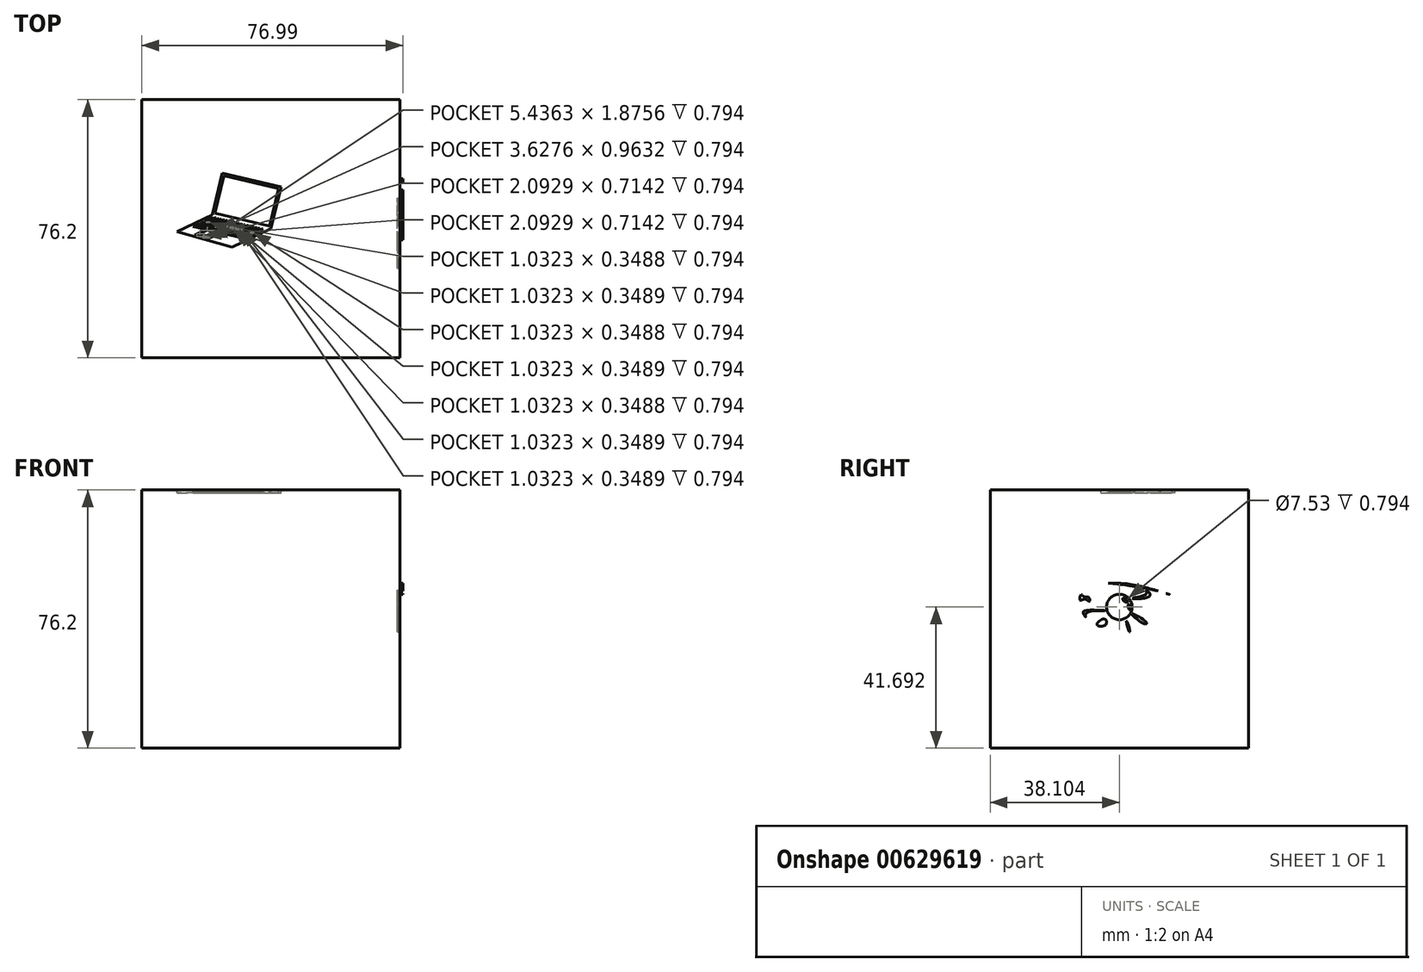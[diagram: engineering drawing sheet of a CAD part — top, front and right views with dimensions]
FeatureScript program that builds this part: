
annotation { "Feature Type Name" : "Feature", "Feature Type Description" : "" }
export const myFeature = defineFeature(function(context is Context, id is Id, definition is map)
    precondition{}
    {
        {
            var Q0;
            Q0=qCreatedBy(makeId("Top.planeOp"),FACE);
            var sketch = newSketch(context, id + "F0", { "sketchPlane" : qUnion([Q0])});
            skLineSegment(sketch, "E0", {"start": v(-11.48, -5.43) * mm, "end": v(0, 0) * mm});
            skLineSegment(sketch, "E1", {"start": v(0, 0) * mm, "end": v(2.93, 12.36) * mm});
            skLineSegment(sketch, "E2", {"start": v(2.93, 12.36) * mm, "end": v(-14.38, 16.45) * mm});
            skLineSegment(sketch, "E3", {"start": v(-14.38, 16.45) * mm, "end": v(-17.3, 4.1) * mm});
            skLineSegment(sketch, "E4", {"start": v(-17.3, 4.1) * mm, "end": v(0, 0) * mm});
            skLineSegment(sketch, "E5", {"start": v(-17.3, 4.1) * mm, "end": v(-27.71, -0.83) * mm});
            skLineSegment(sketch, "E6", {"start": v(-27.71, -0.83) * mm, "end": v(-11.48, -5.43) * mm});
            skLineSegment(sketch, "E7.0", {"start": v(-17.23, 3.43) * mm, "end": v(-16.37, 3.22) * mm});
            skLineSegment(sketch, "E7.1", {"start": v(-17.67, 3.22) * mm, "end": v(-18.38, 2.88) * mm});
            skLineSegment(sketch, "E7.2", {"start": v(-21.88, -1.83) * mm, "end": v(-20.42, -2.24) * mm});
            skLineSegment(sketch, "E7.3", {"start": v(-7.68, -2.93) * mm, "end": v(-6.94, -2.58) * mm});
            skLineSegment(sketch, "E8", {"start": v(-17.67, 3.22) * mm, "end": v(-17.08, 3.08) * mm});
            skLineSegment(sketch, "E9", {"start": v(-17.08, 3.08) * mm, "end": v(-16.64, 3.29) * mm});
            skPoint(sketch, "E10", {"position": v(-17.67, 3.22) * mm});
            skPoint(sketch, "E11", {"position": v(-17.23, 3.43) * mm});
            skPoint(sketch, "E12", {"position": v(-17.08, 3.08) * mm});
            skPoint(sketch, "E13", {"position": v(-16.64, 3.29) * mm});
            skPoint(sketch, "E14.1.0.0", {"position": v(-16.37, 3.22) * mm});
            skLineSegment(sketch, "E14.1.0.1", {"start": v(-16.8, 3.01) * mm, "end": v(-16.22, 2.87) * mm});
            skLineSegment(sketch, "E14.1.0.2", {"start": v(-16.22, 2.87) * mm, "end": v(-15.78, 3.08) * mm});
            skPoint(sketch, "E14.1.0.3", {"position": v(-16.22, 2.87) * mm});
            skPoint(sketch, "E14.1.0.4", {"position": v(-15.78, 3.08) * mm});
            skPoint(sketch, "E14.1.0.5", {"position": v(-16.8, 3.01) * mm});
            skPoint(sketch, "E14.2.0.0", {"position": v(-15.5, 3.02) * mm});
            skLineSegment(sketch, "E14.2.0.1", {"start": v(-15.94, 2.8) * mm, "end": v(-15.35, 2.67) * mm});
            skLineSegment(sketch, "E14.2.0.2", {"start": v(-15.35, 2.67) * mm, "end": v(-14.91, 2.88) * mm});
            skPoint(sketch, "E14.2.0.3", {"position": v(-15.35, 2.67) * mm});
            skPoint(sketch, "E14.2.0.4", {"position": v(-14.91, 2.88) * mm});
            skPoint(sketch, "E14.2.0.5", {"position": v(-15.94, 2.8) * mm});
            skPoint(sketch, "E14.3.0.0", {"position": v(-14.64, 2.81) * mm});
            skLineSegment(sketch, "E14.3.0.1", {"start": v(-15.08, 2.6) * mm, "end": v(-14.49, 2.46) * mm});
            skLineSegment(sketch, "E14.3.0.2", {"start": v(-14.49, 2.46) * mm, "end": v(-14.05, 2.67) * mm});
            skPoint(sketch, "E14.3.0.3", {"position": v(-14.49, 2.46) * mm});
            skPoint(sketch, "E14.3.0.4", {"position": v(-14.05, 2.67) * mm});
            skPoint(sketch, "E14.3.0.5", {"position": v(-15.08, 2.6) * mm});
            skPoint(sketch, "E14.4.0.0", {"position": v(-13.77, 2.6) * mm});
            skLineSegment(sketch, "E14.4.0.1", {"start": v(-14.21, 2.4) * mm, "end": v(-13.62, 2.26) * mm});
            skLineSegment(sketch, "E14.4.0.2", {"start": v(-13.62, 2.26) * mm, "end": v(-13.18, 2.47) * mm});
            skPoint(sketch, "E14.4.0.3", {"position": v(-13.62, 2.26) * mm});
            skPoint(sketch, "E14.4.0.4", {"position": v(-13.18, 2.47) * mm});
            skPoint(sketch, "E14.4.0.5", {"position": v(-14.21, 2.4) * mm});
            skPoint(sketch, "E14.5.0.0", {"position": v(-12.9, 2.4) * mm});
            skLineSegment(sketch, "E14.5.0.1", {"start": v(-13.35, 2.2) * mm, "end": v(-12.76, 2.05) * mm});
            skLineSegment(sketch, "E14.5.0.2", {"start": v(-12.76, 2.05) * mm, "end": v(-12.32, 2.26) * mm});
            skPoint(sketch, "E14.5.0.3", {"position": v(-12.76, 2.05) * mm});
            skPoint(sketch, "E14.5.0.4", {"position": v(-12.32, 2.26) * mm});
            skPoint(sketch, "E14.5.0.5", {"position": v(-13.35, 2.2) * mm});
            skPoint(sketch, "E14.6.0.0", {"position": v(-12.04, 2.2) * mm});
            skLineSegment(sketch, "E14.6.0.1", {"start": v(-12.48, 1.99) * mm, "end": v(-11.9, 1.85) * mm});
            skLineSegment(sketch, "E14.6.0.2", {"start": v(-11.9, 1.85) * mm, "end": v(-11.45, 2.06) * mm});
            skPoint(sketch, "E14.6.0.3", {"position": v(-11.9, 1.85) * mm});
            skPoint(sketch, "E14.6.0.4", {"position": v(-11.45, 2.06) * mm});
            skPoint(sketch, "E14.6.0.5", {"position": v(-12.48, 1.99) * mm});
            skPoint(sketch, "E14.7.0.0", {"position": v(-11.18, 2) * mm});
            skLineSegment(sketch, "E14.7.0.1", {"start": v(-11.62, 1.78) * mm, "end": v(-11.03, 1.64) * mm});
            skLineSegment(sketch, "E14.7.0.2", {"start": v(-11.03, 1.64) * mm, "end": v(-10.58, 1.85) * mm});
            skPoint(sketch, "E14.7.0.3", {"position": v(-11.03, 1.64) * mm});
            skPoint(sketch, "E14.7.0.4", {"position": v(-10.58, 1.85) * mm});
            skPoint(sketch, "E14.7.0.5", {"position": v(-11.62, 1.78) * mm});
            skPoint(sketch, "E14.8.0.0", {"position": v(-10.31, 1.79) * mm});
            skLineSegment(sketch, "E14.8.0.1", {"start": v(-10.75, 1.58) * mm, "end": v(-10.16, 1.44) * mm});
            skLineSegment(sketch, "E14.8.0.2", {"start": v(-10.16, 1.44) * mm, "end": v(-9.72, 1.65) * mm});
            skPoint(sketch, "E14.8.0.3", {"position": v(-10.16, 1.44) * mm});
            skPoint(sketch, "E14.8.0.4", {"position": v(-9.72, 1.65) * mm});
            skPoint(sketch, "E14.8.0.5", {"position": v(-10.75, 1.58) * mm});
            skPoint(sketch, "E14.9.0.0", {"position": v(-9.45, 1.58) * mm});
            skLineSegment(sketch, "E14.9.0.1", {"start": v(-9.89, 1.37) * mm, "end": v(-9.3, 1.23) * mm});
            skLineSegment(sketch, "E14.9.0.2", {"start": v(-9.3, 1.23) * mm, "end": v(-8.85, 1.44) * mm});
            skPoint(sketch, "E14.9.0.3", {"position": v(-9.3, 1.23) * mm});
            skPoint(sketch, "E14.9.0.4", {"position": v(-8.85, 1.44) * mm});
            skPoint(sketch, "E14.9.0.5", {"position": v(-9.89, 1.37) * mm});
            skPoint(sketch, "E14.10.0.0", {"position": v(-8.58, 1.38) * mm});
            skLineSegment(sketch, "E14.10.0.1", {"start": v(-9.02, 1.17) * mm, "end": v(-8.43, 1.03) * mm});
            skLineSegment(sketch, "E14.10.0.2", {"start": v(-8.43, 1.03) * mm, "end": v(-7.99, 1.24) * mm});
            skPoint(sketch, "E14.10.0.3", {"position": v(-8.43, 1.03) * mm});
            skPoint(sketch, "E14.10.0.4", {"position": v(-7.99, 1.24) * mm});
            skPoint(sketch, "E14.10.0.5", {"position": v(-9.02, 1.17) * mm});
            skPoint(sketch, "E14.11.0.0", {"position": v(-7.72, 1.17) * mm});
            skLineSegment(sketch, "E14.11.0.1", {"start": v(-8.16, 0.96) * mm, "end": v(-7.57, 0.83) * mm});
            skLineSegment(sketch, "E14.11.0.2", {"start": v(-7.57, 0.83) * mm, "end": v(-7.12, 1.03) * mm});
            skPoint(sketch, "E14.11.0.3", {"position": v(-7.57, 0.83) * mm});
            skPoint(sketch, "E14.11.0.4", {"position": v(-7.12, 1.03) * mm});
            skPoint(sketch, "E14.11.0.5", {"position": v(-8.16, 0.96) * mm});
            skPoint(sketch, "E14.12.0.0", {"position": v(-6.85, 0.97) * mm});
            skLineSegment(sketch, "E14.12.0.1", {"start": v(-7.3, 0.76) * mm, "end": v(-6.7, 0.62) * mm});
            skLineSegment(sketch, "E14.12.0.2", {"start": v(-6.7, 0.62) * mm, "end": v(-6.26, 0.83) * mm});
            skPoint(sketch, "E14.12.0.3", {"position": v(-6.7, 0.62) * mm});
            skPoint(sketch, "E14.12.0.4", {"position": v(-6.26, 0.83) * mm});
            skPoint(sketch, "E14.12.0.5", {"position": v(-7.3, 0.76) * mm});
            skPoint(sketch, "E14.13.0.0", {"position": v(-5.99, 0.76) * mm});
            skLineSegment(sketch, "E14.13.0.1", {"start": v(-6.43, 0.56) * mm, "end": v(-5.84, 0.42) * mm});
            skLineSegment(sketch, "E14.13.0.2", {"start": v(-5.84, 0.42) * mm, "end": v(-5.4, 0.62) * mm});
            skPoint(sketch, "E14.13.0.3", {"position": v(-5.84, 0.42) * mm});
            skPoint(sketch, "E14.13.0.4", {"position": v(-5.4, 0.62) * mm});
            skPoint(sketch, "E14.13.0.5", {"position": v(-6.43, 0.56) * mm});
            skPoint(sketch, "E14.14.0.0", {"position": v(-5.12, 0.56) * mm});
            skLineSegment(sketch, "E14.14.0.1", {"start": v(-5.56, 0.35) * mm, "end": v(-4.97, 0.21) * mm});
            skLineSegment(sketch, "E14.14.0.2", {"start": v(-4.97, 0.21) * mm, "end": v(-4.53, 0.42) * mm});
            skPoint(sketch, "E14.14.0.3", {"position": v(-4.97, 0.21) * mm});
            skPoint(sketch, "E14.14.0.4", {"position": v(-4.53, 0.42) * mm});
            skPoint(sketch, "E14.14.0.5", {"position": v(-5.56, 0.35) * mm});
            skPoint(sketch, "E14.15.0.0", {"position": v(-4.26, 0.35) * mm});
            skLineSegment(sketch, "E14.15.0.1", {"start": v(-4.7, 0.15) * mm, "end": v(-4.1, 0) * mm});
            skLineSegment(sketch, "E14.15.0.2", {"start": v(-4.1, 0) * mm, "end": v(-3.66, 0.21) * mm});
            skPoint(sketch, "E14.15.0.3", {"position": v(-4.1, 0) * mm});
            skPoint(sketch, "E14.15.0.4", {"position": v(-3.66, 0.21) * mm});
            skPoint(sketch, "E14.15.0.5", {"position": v(-4.7, 0.15) * mm});
            skPoint(sketch, "E14.16.0.0", {"position": v(-3.39, 0.15) * mm});
            skLineSegment(sketch, "E14.16.0.1", {"start": v(-3.83, -0.06) * mm, "end": v(-3.24, -0.2) * mm});
            skLineSegment(sketch, "E14.16.0.2", {"start": v(-3.24, -0.2) * mm, "end": v(-2.8, 0.01) * mm});
            skPoint(sketch, "E14.16.0.3", {"position": v(-3.24, -0.2) * mm});
            skPoint(sketch, "E14.16.0.4", {"position": v(-2.8, 0.01) * mm});
            skPoint(sketch, "E14.16.0.5", {"position": v(-3.83, -0.06) * mm});
            skPoint(sketch, "E14.17.0.0", {"position": v(-2.52, -0.05) * mm});
            skLineSegment(sketch, "E14.17.0.1", {"start": v(-2.97, -0.26) * mm, "end": v(-2.38, -0.4) * mm});
            skPoint(sketch, "E14.17.0.3", {"position": v(-2.38, -0.4) * mm});
            skPoint(sketch, "E14.17.0.4", {"position": v(-1.93, -0.2) * mm});
            skPoint(sketch, "E14.17.0.5", {"position": v(-2.97, -0.26) * mm});
            skLineSegment(sketch, "E14.direction1", {"start": v(-16.64, 3.29) * mm, "end": v(-16.37, 3.22) * mm, "construction": true});
            skLineSegment(sketch, "E15", {"start": v(-16.8, 3.01) * mm, "end": v(-16.37, 3.22) * mm});
            skLineSegment(sketch, "E16", {"start": v(-15.94, 2.8) * mm, "end": v(-15.5, 3.02) * mm});
            skLineSegment(sketch, "E17", {"start": v(-15.08, 2.6) * mm, "end": v(-14.64, 2.81) * mm});
            skLineSegment(sketch, "E18", {"start": v(-14.21, 2.4) * mm, "end": v(-13.77, 2.6) * mm});
            skLineSegment(sketch, "E19", {"start": v(-13.35, 2.2) * mm, "end": v(-12.9, 2.4) * mm});
            skLineSegment(sketch, "E20", {"start": v(-12.48, 1.99) * mm, "end": v(-12.04, 2.2) * mm});
            skLineSegment(sketch, "E21", {"start": v(-11.62, 1.78) * mm, "end": v(-11.18, 2) * mm});
            skLineSegment(sketch, "E22", {"start": v(-10.75, 1.58) * mm, "end": v(-10.31, 1.79) * mm});
            skLineSegment(sketch, "E23", {"start": v(-9.89, 1.37) * mm, "end": v(-9.45, 1.58) * mm});
            skLineSegment(sketch, "E24", {"start": v(-9.02, 1.17) * mm, "end": v(-8.58, 1.38) * mm});
            skLineSegment(sketch, "E25", {"start": v(-8.16, 0.96) * mm, "end": v(-7.72, 1.17) * mm});
            skLineSegment(sketch, "E26", {"start": v(-7.3, 0.76) * mm, "end": v(-6.85, 0.97) * mm});
            skLineSegment(sketch, "E27", {"start": v(-6.43, 0.56) * mm, "end": v(-5.99, 0.76) * mm});
            skLineSegment(sketch, "E28", {"start": v(-5.56, 0.35) * mm, "end": v(-5.12, 0.56) * mm});
            skLineSegment(sketch, "E29", {"start": v(-4.7, 0.15) * mm, "end": v(-4.26, 0.35) * mm});
            skLineSegment(sketch, "E30", {"start": v(-3.83, -0.06) * mm, "end": v(-3.39, 0.15) * mm});
            skLineSegment(sketch, "E31", {"start": v(-2.97, -0.26) * mm, "end": v(-2.52, -0.05) * mm});
            skLineSegment(sketch, "E32", {"start": v(-2.38, -0.4) * mm, "end": v(-2.35, -0.4) * mm});
            skPoint(sketch, "E33.1.0.0", {"position": v(-13.9, 1.51) * mm});
            skPoint(sketch, "E33.1.0.1", {"position": v(-14.33, 1.92) * mm});
            skLineSegment(sketch, "E33.1.0.2", {"start": v(-11.9, 1.04) * mm, "end": v(-11.3, 0.9) * mm});
            skPoint(sketch, "E33.1.0.3", {"position": v(-17.36, 2.33) * mm});
            skPoint(sketch, "E33.1.0.4", {"position": v(-10.44, 0.7) * mm});
            skPoint(sketch, "E33.1.0.5", {"position": v(-18.23, 2.53) * mm});
            skPoint(sketch, "E33.1.0.6", {"position": v(-9.3, 0.42) * mm});
            skPoint(sketch, "E33.1.0.7", {"position": v(-16.23, 2.06) * mm});
            skPoint(sketch, "E33.1.0.8", {"position": v(-12.77, 1.24) * mm});
            skPoint(sketch, "E33.1.0.9", {"position": v(-14.5, 1.65) * mm});
            skPoint(sketch, "E33.1.0.10", {"position": v(-17.96, 2.47) * mm});
            skLineSegment(sketch, "E33.1.0.11", {"start": v(-15.36, 1.86) * mm, "end": v(-14.77, 1.72) * mm});
            skLineSegment(sketch, "E33.1.0.12", {"start": v(-12.77, 1.24) * mm, "end": v(-12.17, 1.1) * mm});
            skPoint(sketch, "E33.1.0.13", {"position": v(-14.92, 2.06) * mm});
            skPoint(sketch, "E33.1.0.14", {"position": v(-11.46, 1.24) * mm});
            skPoint(sketch, "E33.1.0.15", {"position": v(-11.3, 0.9) * mm});
            skPoint(sketch, "E33.1.0.16", {"position": v(-18.82, 2.67) * mm});
            skLineSegment(sketch, "E33.1.0.17", {"start": v(-11.03, 0.83) * mm, "end": v(-10.6, 1.04) * mm});
            skLineSegment(sketch, "E33.1.0.18", {"start": v(-13.63, 1.45) * mm, "end": v(-13.04, 1.3) * mm});
            skPoint(sketch, "E33.1.0.19", {"position": v(-16.92, 2.54) * mm});
            skPoint(sketch, "E33.1.0.20", {"position": v(-13.46, 1.72) * mm});
            skPoint(sketch, "E33.1.0.21", {"position": v(-11.03, 0.83) * mm});
            skPoint(sketch, "E33.1.0.22", {"position": v(-15.2, 2.13) * mm});
            skPoint(sketch, "E33.1.0.23", {"position": v(-16.06, 2.33) * mm});
            skPoint(sketch, "E33.1.0.24", {"position": v(-11.73, 1.3) * mm});
            skLineSegment(sketch, "E33.1.0.25", {"start": v(-16.23, 2.06) * mm, "end": v(-15.63, 1.92) * mm});
            skPoint(sketch, "E33.1.0.26", {"position": v(-12.6, 1.51) * mm});
            skPoint(sketch, "E33.1.0.27", {"position": v(-16.65, 2.47) * mm});
            skPoint(sketch, "E33.1.0.28", {"position": v(-13.19, 1.65) * mm});
            skPoint(sketch, "E33.1.0.29", {"position": v(-16.5, 2.12) * mm});
            skPoint(sketch, "E33.1.0.30", {"position": v(-13.04, 1.3) * mm});
            skLineSegment(sketch, "E33.1.0.31", {"start": v(-11.3, 0.9) * mm, "end": v(-10.87, 1.1) * mm});
            skPoint(sketch, "E33.1.0.32", {"position": v(-9.58, 0.49) * mm});
            skLineSegment(sketch, "E33.1.0.33", {"start": v(-11.03, 0.83) * mm, "end": v(-10.44, 0.7) * mm});
            skPoint(sketch, "E33.1.0.34", {"position": v(-14.77, 1.72) * mm});
            skPoint(sketch, "E33.1.0.35", {"position": v(-17.1, 2.26) * mm});
            skPoint(sketch, "E33.1.0.36", {"position": v(-13.63, 1.45) * mm});
            skLineSegment(sketch, "E33.1.0.37", {"start": v(-17.1, 2.26) * mm, "end": v(-16.5, 2.12) * mm});
            skLineSegment(sketch, "E33.1.0.38", {"start": v(-14.5, 1.65) * mm, "end": v(-13.9, 1.51) * mm});
            skPoint(sketch, "E33.1.0.39", {"position": v(-10.17, 0.63) * mm});
            skLineSegment(sketch, "E33.1.0.40", {"start": v(-17.96, 2.47) * mm, "end": v(-17.36, 2.33) * mm});
            skLineSegment(sketch, "E33.1.0.41", {"start": v(-10.17, 0.63) * mm, "end": v(-9.58, 0.49) * mm});
            skPoint(sketch, "E33.1.0.42", {"position": v(-14.05, 1.86) * mm});
            skPoint(sketch, "E33.1.0.43", {"position": v(-15.63, 1.92) * mm});
            skPoint(sketch, "E33.1.0.44", {"position": v(-15.78, 2.27) * mm});
            skPoint(sketch, "E33.1.0.45", {"position": v(-12.32, 1.45) * mm});
            skPoint(sketch, "E33.1.0.46", {"position": v(-15.36, 1.86) * mm});
            skPoint(sketch, "E33.1.0.47", {"position": v(-12.17, 1.1) * mm});
            skPoint(sketch, "E33.1.0.48", {"position": v(-11.9, 1.04) * mm});
            skPoint(sketch, "E33.1.0.49", {"position": v(-17.51, 2.68) * mm});
            skPoint(sketch, "E33.1.0.50", {"position": v(-18.38, 2.88) * mm});
            skPoint(sketch, "E33.1.0.51", {"position": v(-17.79, 2.74) * mm});
            skLineSegment(sketch, "E33.1.0.52", {"start": v(-13.04, 1.3) * mm, "end": v(-12.6, 1.51) * mm});
            skPoint(sketch, "E33.1.0.53", {"position": v(-9.14, 0.7) * mm});
            skLineSegment(sketch, "E33.1.0.54", {"start": v(-17.1, 2.26) * mm, "end": v(-16.65, 2.47) * mm});
            skLineSegment(sketch, "E33.1.0.55", {"start": v(-16.5, 2.12) * mm, "end": v(-16.06, 2.33) * mm});
            skLineSegment(sketch, "E33.1.0.56", {"start": v(-17.96, 2.47) * mm, "end": v(-17.51, 2.68) * mm});
            skLineSegment(sketch, "E33.1.0.57", {"start": v(-12.77, 1.24) * mm, "end": v(-12.32, 1.45) * mm});
            skLineSegment(sketch, "E33.1.0.58", {"start": v(-14.77, 1.72) * mm, "end": v(-14.33, 1.92) * mm});
            skLineSegment(sketch, "E33.1.0.59", {"start": v(-18.23, 2.53) * mm, "end": v(-17.79, 2.74) * mm});
            skLineSegment(sketch, "E33.1.0.60", {"start": v(-15.63, 1.92) * mm, "end": v(-15.2, 2.13) * mm});
            skLineSegment(sketch, "E33.1.0.61", {"start": v(-14.5, 1.65) * mm, "end": v(-14.05, 1.86) * mm});
            skLineSegment(sketch, "E33.1.0.62", {"start": v(-12.17, 1.1) * mm, "end": v(-11.73, 1.3) * mm});
            skLineSegment(sketch, "E33.1.0.63", {"start": v(-15.36, 1.86) * mm, "end": v(-14.92, 2.06) * mm});
            skLineSegment(sketch, "E33.1.0.64", {"start": v(-16.23, 2.06) * mm, "end": v(-15.78, 2.27) * mm});
            skLineSegment(sketch, "E33.1.0.65", {"start": v(-13.63, 1.45) * mm, "end": v(-13.19, 1.65) * mm});
            skLineSegment(sketch, "E33.1.0.66", {"start": v(-17.36, 2.33) * mm, "end": v(-16.92, 2.54) * mm});
            skLineSegment(sketch, "E33.1.0.67", {"start": v(-11.9, 1.04) * mm, "end": v(-11.46, 1.24) * mm});
            skLineSegment(sketch, "E33.1.0.68", {"start": v(-13.9, 1.51) * mm, "end": v(-13.46, 1.72) * mm});
            skPoint(sketch, "E33.1.0.69", {"position": v(-8.86, 0.63) * mm});
            skLineSegment(sketch, "E33.1.0.70", {"start": v(-18.82, 2.67) * mm, "end": v(-18.23, 2.53) * mm});
            skPoint(sketch, "E33.1.0.71", {"position": v(-10.87, 1.1) * mm});
            skPoint(sketch, "E33.1.0.72", {"position": v(-10.6, 1.04) * mm});
            skLineSegment(sketch, "E33.1.0.73", {"start": v(-10.44, 0.7) * mm, "end": v(-10, 0.9) * mm});
            skPoint(sketch, "E33.1.0.74", {"position": v(-10, 0.9) * mm});
            skPoint(sketch, "E33.1.0.75", {"position": v(-9.73, 0.84) * mm});
            skLineSegment(sketch, "E33.1.0.76", {"start": v(-10.17, 0.63) * mm, "end": v(-9.73, 0.84) * mm});
            skLineSegment(sketch, "E33.1.0.77", {"start": v(-9.58, 0.49) * mm, "end": v(-9.14, 0.7) * mm});
            skLineSegment(sketch, "E33.1.0.78", {"start": v(-9.3, 0.42) * mm, "end": v(-8.86, 0.63) * mm});
            skLineSegment(sketch, "E33.1.0.79", {"start": v(-9.3, 0.42) * mm, "end": v(-8.71, 0.28) * mm});
            skLineSegment(sketch, "E33.1.0.80", {"start": v(-8.71, 0.28) * mm, "end": v(-8.27, 0.5) * mm});
            skLineSegment(sketch, "E33.1.0.81", {"start": v(-8.44, 0.22) * mm, "end": v(-8, 0.43) * mm});
            skLineSegment(sketch, "E33.1.0.82", {"start": v(-8.44, 0.22) * mm, "end": v(-7.85, 0.08) * mm});
            skLineSegment(sketch, "E33.1.0.83", {"start": v(-7.85, 0.08) * mm, "end": v(-7.4, 0.29) * mm});
            skPoint(sketch, "E33.1.0.84", {"position": v(-7.85, 0.08) * mm});
            skPoint(sketch, "E33.1.0.85", {"position": v(-8.44, 0.22) * mm});
            skPoint(sketch, "E33.1.0.86", {"position": v(-8.71, 0.28) * mm});
            skPoint(sketch, "E33.1.0.87", {"position": v(-8.27, 0.5) * mm});
            skPoint(sketch, "E33.1.0.88", {"position": v(-8, 0.43) * mm});
            skPoint(sketch, "E33.1.0.89", {"position": v(-7.4, 0.29) * mm});
            skPoint(sketch, "E33.1.0.90", {"position": v(-6.54, 0.08) * mm});
            skPoint(sketch, "E33.1.0.91", {"position": v(-5.84, -0.4) * mm});
            skLineSegment(sketch, "E33.1.0.92", {"start": v(-7.57, 0.01) * mm, "end": v(-7.13, 0.22) * mm});
            skLineSegment(sketch, "E33.1.0.93", {"start": v(-4.98, -0.6) * mm, "end": v(-4.39, -0.74) * mm});
            skLineSegment(sketch, "E33.1.0.94", {"start": v(-6.12, -0.33) * mm, "end": v(-5.68, -0.12) * mm});
            skLineSegment(sketch, "E33.1.0.95", {"start": v(-5.84, -0.4) * mm, "end": v(-5.25, -0.54) * mm});
            skPoint(sketch, "E33.1.0.96", {"position": v(-4.11, -0.8) * mm});
            skLineSegment(sketch, "E33.1.0.97", {"start": v(-5.25, -0.54) * mm, "end": v(-4.81, -0.33) * mm});
            skPoint(sketch, "E33.1.0.98", {"position": v(-6.27, 0.02) * mm});
            skPoint(sketch, "E33.1.0.99", {"position": v(-5.68, -0.12) * mm});
            skPoint(sketch, "E33.1.0.100", {"position": v(-6.12, -0.33) * mm});
            skPoint(sketch, "E33.1.0.101", {"position": v(-4.39, -0.74) * mm});
            skLineSegment(sketch, "E33.1.0.102", {"start": v(-4.98, -0.6) * mm, "end": v(-4.54, -0.4) * mm});
            skLineSegment(sketch, "E33.1.0.103", {"start": v(-4.11, -0.8) * mm, "end": v(-3.52, -0.95) * mm});
            skLineSegment(sketch, "E33.1.0.104", {"start": v(-6.98, -0.13) * mm, "end": v(-6.54, 0.08) * mm});
            skLineSegment(sketch, "E33.1.0.105", {"start": v(-4.11, -0.8) * mm, "end": v(-3.67, -0.6) * mm});
            skLineSegment(sketch, "E33.1.0.106", {"start": v(-4.39, -0.74) * mm, "end": v(-3.95, -0.53) * mm});
            skLineSegment(sketch, "E33.1.0.107", {"start": v(-6.7, -0.2) * mm, "end": v(-6.27, 0.02) * mm});
            skLineSegment(sketch, "E33.1.0.108", {"start": v(-5.84, -0.4) * mm, "end": v(-5.4, -0.19) * mm});
            skPoint(sketch, "E33.1.0.109", {"position": v(-7.13, 0.22) * mm});
            skPoint(sketch, "E33.1.0.110", {"position": v(-5.4, -0.19) * mm});
            skPoint(sketch, "E33.1.0.111", {"position": v(-5.25, -0.54) * mm});
            skPoint(sketch, "E33.1.0.112", {"position": v(-4.98, -0.6) * mm});
            skLineSegment(sketch, "E33.1.0.113", {"start": v(-6.7, -0.2) * mm, "end": v(-6.12, -0.33) * mm});
            skPoint(sketch, "E33.1.0.114", {"position": v(-6.7, -0.2) * mm});
            skPoint(sketch, "E33.1.0.115", {"position": v(-6.98, -0.13) * mm});
            skLineSegment(sketch, "E33.1.0.116", {"start": v(-7.57, 0.01) * mm, "end": v(-6.98, -0.13) * mm});
            skPoint(sketch, "E33.1.0.117", {"position": v(-7.57, 0.01) * mm});
            skPoint(sketch, "E33.1.0.118", {"position": v(-4.81, -0.33) * mm});
            skPoint(sketch, "E33.1.0.119", {"position": v(-4.54, -0.4) * mm});
            skPoint(sketch, "E33.1.0.120", {"position": v(-3.95, -0.53) * mm});
            skPoint(sketch, "E33.1.0.121", {"position": v(-3.67, -0.6) * mm});
            skPoint(sketch, "E33.1.0.122", {"position": v(-3.52, -0.95) * mm});
            skPoint(sketch, "E33.1.0.123", {"position": v(-3.08, -0.74) * mm});
            skPoint(sketch, "E33.2.0.0", {"position": v(-15.05, 0.97) * mm});
            skPoint(sketch, "E33.2.0.1", {"position": v(-15.48, 1.38) * mm});
            skLineSegment(sketch, "E33.2.0.2", {"start": v(-13.05, 0.5) * mm, "end": v(-12.46, 0.35) * mm});
            skPoint(sketch, "E33.2.0.3", {"position": v(-18.51, 1.79) * mm});
            skPoint(sketch, "E33.2.0.4", {"position": v(-11.6, 0.15) * mm});
            skPoint(sketch, "E33.2.0.5", {"position": v(-19.38, 2) * mm});
            skPoint(sketch, "E33.2.0.6", {"position": v(-10.45, -0.12) * mm});
            skPoint(sketch, "E33.2.0.7", {"position": v(-17.37, 1.52) * mm});
            skPoint(sketch, "E33.2.0.8", {"position": v(-13.91, 0.7) * mm});
            skPoint(sketch, "E33.2.0.9", {"position": v(-15.64, 1.1) * mm});
            skPoint(sketch, "E33.2.0.10", {"position": v(-19.1, 1.93) * mm});
            skLineSegment(sketch, "E33.2.0.11", {"start": v(-16.5, 1.31) * mm, "end": v(-15.92, 1.17) * mm});
            skLineSegment(sketch, "E33.2.0.12", {"start": v(-13.91, 0.7) * mm, "end": v(-13.32, 0.56) * mm});
            skPoint(sketch, "E33.2.0.13", {"position": v(-16.07, 1.52) * mm});
            skPoint(sketch, "E33.2.0.14", {"position": v(-12.6, 0.7) * mm});
            skPoint(sketch, "E33.2.0.15", {"position": v(-12.46, 0.35) * mm});
            skPoint(sketch, "E33.2.0.16", {"position": v(-19.97, 2.13) * mm});
            skLineSegment(sketch, "E33.2.0.17", {"start": v(-12.18, 0.29) * mm, "end": v(-11.74, 0.5) * mm});
            skLineSegment(sketch, "E33.2.0.18", {"start": v(-14.78, 0.9) * mm, "end": v(-14.19, 0.76) * mm});
            skPoint(sketch, "E33.2.0.19", {"position": v(-18.07, 2) * mm});
            skPoint(sketch, "E33.2.0.20", {"position": v(-14.61, 1.18) * mm});
            skPoint(sketch, "E33.2.0.21", {"position": v(-12.18, 0.29) * mm});
            skPoint(sketch, "E33.2.0.22", {"position": v(-16.34, 1.59) * mm});
            skPoint(sketch, "E33.2.0.23", {"position": v(-17.2, 1.8) * mm});
            skPoint(sketch, "E33.2.0.24", {"position": v(-12.88, 0.77) * mm});
            skLineSegment(sketch, "E33.2.0.25", {"start": v(-17.37, 1.52) * mm, "end": v(-16.78, 1.38) * mm});
            skPoint(sketch, "E33.2.0.26", {"position": v(-13.75, 0.97) * mm});
            skPoint(sketch, "E33.2.0.27", {"position": v(-17.8, 1.93) * mm});
            skPoint(sketch, "E33.2.0.28", {"position": v(-14.34, 1.11) * mm});
            skPoint(sketch, "E33.2.0.29", {"position": v(-17.65, 1.58) * mm});
            skPoint(sketch, "E33.2.0.30", {"position": v(-14.19, 0.76) * mm});
            skLineSegment(sketch, "E33.2.0.31", {"start": v(-12.46, 0.35) * mm, "end": v(-12.02, 0.56) * mm});
            skPoint(sketch, "E33.2.0.32", {"position": v(-10.73, -0.06) * mm});
            skLineSegment(sketch, "E33.2.0.33", {"start": v(-12.18, 0.29) * mm, "end": v(-11.6, 0.15) * mm});
            skPoint(sketch, "E33.2.0.34", {"position": v(-15.92, 1.17) * mm});
            skPoint(sketch, "E33.2.0.35", {"position": v(-18.24, 1.72) * mm});
            skPoint(sketch, "E33.2.0.36", {"position": v(-14.78, 0.9) * mm});
            skLineSegment(sketch, "E33.2.0.37", {"start": v(-18.24, 1.72) * mm, "end": v(-17.65, 1.58) * mm});
            skLineSegment(sketch, "E33.2.0.38", {"start": v(-15.64, 1.1) * mm, "end": v(-15.05, 0.97) * mm});
            skPoint(sketch, "E33.2.0.39", {"position": v(-11.32, 0.08) * mm});
            skLineSegment(sketch, "E33.2.0.40", {"start": v(-19.1, 1.93) * mm, "end": v(-18.51, 1.79) * mm});
            skLineSegment(sketch, "E33.2.0.41", {"start": v(-11.32, 0.08) * mm, "end": v(-10.73, -0.06) * mm});
            skPoint(sketch, "E33.2.0.42", {"position": v(-15.2, 1.32) * mm});
            skPoint(sketch, "E33.2.0.43", {"position": v(-16.78, 1.38) * mm});
            skPoint(sketch, "E33.2.0.44", {"position": v(-16.93, 1.73) * mm});
            skPoint(sketch, "E33.2.0.45", {"position": v(-13.47, 0.9) * mm});
            skPoint(sketch, "E33.2.0.46", {"position": v(-16.5, 1.31) * mm});
            skPoint(sketch, "E33.2.0.47", {"position": v(-13.32, 0.56) * mm});
            skPoint(sketch, "E33.2.0.48", {"position": v(-13.05, 0.5) * mm});
            skPoint(sketch, "E33.2.0.49", {"position": v(-18.66, 2.13) * mm});
            skPoint(sketch, "E33.2.0.50", {"position": v(-19.53, 2.34) * mm});
            skPoint(sketch, "E33.2.0.51", {"position": v(-18.94, 2.2) * mm});
            skLineSegment(sketch, "E33.2.0.52", {"start": v(-14.19, 0.76) * mm, "end": v(-13.75, 0.97) * mm});
            skPoint(sketch, "E33.2.0.53", {"position": v(-10.29, 0.15) * mm});
            skLineSegment(sketch, "E33.2.0.54", {"start": v(-18.24, 1.72) * mm, "end": v(-17.8, 1.93) * mm});
            skLineSegment(sketch, "E33.2.0.55", {"start": v(-17.65, 1.58) * mm, "end": v(-17.2, 1.8) * mm});
            skLineSegment(sketch, "E33.2.0.56", {"start": v(-19.1, 1.93) * mm, "end": v(-18.66, 2.13) * mm});
            skLineSegment(sketch, "E33.2.0.57", {"start": v(-13.91, 0.7) * mm, "end": v(-13.47, 0.9) * mm});
            skLineSegment(sketch, "E33.2.0.58", {"start": v(-15.92, 1.17) * mm, "end": v(-15.48, 1.38) * mm});
            skLineSegment(sketch, "E33.2.0.59", {"start": v(-19.38, 2) * mm, "end": v(-18.94, 2.2) * mm});
            skLineSegment(sketch, "E33.2.0.60", {"start": v(-16.78, 1.38) * mm, "end": v(-16.34, 1.59) * mm});
            skLineSegment(sketch, "E33.2.0.61", {"start": v(-15.64, 1.1) * mm, "end": v(-15.2, 1.32) * mm});
            skLineSegment(sketch, "E33.2.0.62", {"start": v(-13.32, 0.56) * mm, "end": v(-12.88, 0.77) * mm});
            skLineSegment(sketch, "E33.2.0.63", {"start": v(-16.5, 1.31) * mm, "end": v(-16.07, 1.52) * mm});
            skLineSegment(sketch, "E33.2.0.64", {"start": v(-17.37, 1.52) * mm, "end": v(-16.93, 1.73) * mm});
            skLineSegment(sketch, "E33.2.0.65", {"start": v(-14.78, 0.9) * mm, "end": v(-14.34, 1.11) * mm});
            skLineSegment(sketch, "E33.2.0.66", {"start": v(-18.51, 1.79) * mm, "end": v(-18.07, 2) * mm});
            skLineSegment(sketch, "E33.2.0.67", {"start": v(-13.05, 0.5) * mm, "end": v(-12.6, 0.7) * mm});
            skLineSegment(sketch, "E33.2.0.68", {"start": v(-15.05, 0.97) * mm, "end": v(-14.61, 1.18) * mm});
            skPoint(sketch, "E33.2.0.69", {"position": v(-10.01, 0.09) * mm});
            skLineSegment(sketch, "E33.2.0.70", {"start": v(-19.97, 2.13) * mm, "end": v(-19.38, 2) * mm});
            skPoint(sketch, "E33.2.0.71", {"position": v(-12.02, 0.56) * mm});
            skPoint(sketch, "E33.2.0.72", {"position": v(-11.74, 0.5) * mm});
            skLineSegment(sketch, "E33.2.0.73", {"start": v(-11.6, 0.15) * mm, "end": v(-11.15, 0.36) * mm});
            skPoint(sketch, "E33.2.0.74", {"position": v(-11.15, 0.36) * mm});
            skPoint(sketch, "E33.2.0.75", {"position": v(-10.88, 0.3) * mm});
            skLineSegment(sketch, "E33.2.0.76", {"start": v(-11.32, 0.08) * mm, "end": v(-10.88, 0.3) * mm});
            skLineSegment(sketch, "E33.2.0.77", {"start": v(-10.73, -0.06) * mm, "end": v(-10.29, 0.15) * mm});
            skLineSegment(sketch, "E33.2.0.78", {"start": v(-10.45, -0.12) * mm, "end": v(-10.01, 0.09) * mm});
            skLineSegment(sketch, "E33.2.0.79", {"start": v(-10.45, -0.12) * mm, "end": v(-9.86, -0.26) * mm});
            skLineSegment(sketch, "E33.2.0.80", {"start": v(-9.86, -0.26) * mm, "end": v(-9.42, -0.05) * mm});
            skLineSegment(sketch, "E33.2.0.81", {"start": v(-9.59, -0.33) * mm, "end": v(-9.15, -0.12) * mm});
            skLineSegment(sketch, "E33.2.0.82", {"start": v(-9.59, -0.33) * mm, "end": v(-9, -0.47) * mm});
            skLineSegment(sketch, "E33.2.0.83", {"start": v(-9, -0.47) * mm, "end": v(-8.56, -0.26) * mm});
            skPoint(sketch, "E33.2.0.84", {"position": v(-9, -0.47) * mm});
            skPoint(sketch, "E33.2.0.85", {"position": v(-9.59, -0.33) * mm});
            skPoint(sketch, "E33.2.0.86", {"position": v(-9.86, -0.26) * mm});
            skPoint(sketch, "E33.2.0.87", {"position": v(-9.42, -0.05) * mm});
            skPoint(sketch, "E33.2.0.88", {"position": v(-9.15, -0.12) * mm});
            skPoint(sketch, "E33.2.0.89", {"position": v(-8.56, -0.26) * mm});
            skPoint(sketch, "E33.2.0.90", {"position": v(-7.7, -0.46) * mm});
            skPoint(sketch, "E33.2.0.91", {"position": v(-7, -0.94) * mm});
            skLineSegment(sketch, "E33.2.0.92", {"start": v(-8.72, -0.53) * mm, "end": v(-8.28, -0.32) * mm});
            skLineSegment(sketch, "E33.2.0.93", {"start": v(-6.13, -1.15) * mm, "end": v(-5.54, -1.29) * mm});
            skLineSegment(sketch, "E33.2.0.94", {"start": v(-7.27, -0.88) * mm, "end": v(-6.83, -0.67) * mm});
            skLineSegment(sketch, "E33.2.0.95", {"start": v(-7, -0.94) * mm, "end": v(-6.4, -1.08) * mm});
            skPoint(sketch, "E33.2.0.96", {"position": v(-5.26, -1.35) * mm});
            skLineSegment(sketch, "E33.2.0.97", {"start": v(-6.4, -1.08) * mm, "end": v(-5.96, -0.87) * mm});
            skPoint(sketch, "E33.2.0.98", {"position": v(-7.42, -0.53) * mm});
            skPoint(sketch, "E33.2.0.99", {"position": v(-6.83, -0.67) * mm});
            skPoint(sketch, "E33.2.0.100", {"position": v(-7.27, -0.88) * mm});
            skPoint(sketch, "E33.2.0.101", {"position": v(-5.54, -1.29) * mm});
            skLineSegment(sketch, "E33.2.0.102", {"start": v(-6.13, -1.15) * mm, "end": v(-5.69, -0.94) * mm});
            skLineSegment(sketch, "E33.2.0.103", {"start": v(-5.26, -1.35) * mm, "end": v(-4.67, -1.5) * mm});
            skLineSegment(sketch, "E33.2.0.104", {"start": v(-8.13, -0.67) * mm, "end": v(-7.7, -0.46) * mm});
            skLineSegment(sketch, "E33.2.0.105", {"start": v(-5.26, -1.35) * mm, "end": v(-4.82, -1.14) * mm});
            skLineSegment(sketch, "E33.2.0.106", {"start": v(-5.54, -1.29) * mm, "end": v(-5.1, -1.08) * mm});
            skLineSegment(sketch, "E33.2.0.107", {"start": v(-7.86, -0.74) * mm, "end": v(-7.42, -0.53) * mm});
            skLineSegment(sketch, "E33.2.0.108", {"start": v(-7, -0.94) * mm, "end": v(-6.55, -0.73) * mm});
            skPoint(sketch, "E33.2.0.109", {"position": v(-8.28, -0.32) * mm});
            skPoint(sketch, "E33.2.0.110", {"position": v(-6.55, -0.73) * mm});
            skPoint(sketch, "E33.2.0.111", {"position": v(-6.4, -1.08) * mm});
            skPoint(sketch, "E33.2.0.112", {"position": v(-6.13, -1.15) * mm});
            skLineSegment(sketch, "E33.2.0.113", {"start": v(-7.86, -0.74) * mm, "end": v(-7.27, -0.88) * mm});
            skPoint(sketch, "E33.2.0.114", {"position": v(-7.86, -0.74) * mm});
            skPoint(sketch, "E33.2.0.115", {"position": v(-8.13, -0.67) * mm});
            skLineSegment(sketch, "E33.2.0.116", {"start": v(-8.72, -0.53) * mm, "end": v(-8.13, -0.67) * mm});
            skPoint(sketch, "E33.2.0.117", {"position": v(-8.72, -0.53) * mm});
            skPoint(sketch, "E33.2.0.118", {"position": v(-5.96, -0.87) * mm});
            skPoint(sketch, "E33.2.0.119", {"position": v(-5.69, -0.94) * mm});
            skPoint(sketch, "E33.2.0.120", {"position": v(-5.1, -1.08) * mm});
            skPoint(sketch, "E33.2.0.121", {"position": v(-4.82, -1.14) * mm});
            skPoint(sketch, "E33.2.0.122", {"position": v(-4.67, -1.5) * mm});
            skPoint(sketch, "E33.2.0.123", {"position": v(-4.23, -1.28) * mm});
            skPoint(sketch, "E33.3.0.0", {"position": v(-16.2, 0.42) * mm});
            skPoint(sketch, "E33.3.0.1", {"position": v(-16.62, 0.84) * mm});
            skLineSegment(sketch, "E33.3.0.2", {"start": v(-14.2, -0.05) * mm, "end": v(-13.6, -0.2) * mm});
            skPoint(sketch, "E33.3.0.3", {"position": v(-19.66, 1.24) * mm});
            skPoint(sketch, "E33.3.0.4", {"position": v(-12.74, -0.4) * mm});
            skPoint(sketch, "E33.3.0.5", {"position": v(-20.53, 1.45) * mm});
            skPoint(sketch, "E33.3.0.6", {"position": v(-11.6, -0.67) * mm});
            skPoint(sketch, "E33.3.0.7", {"position": v(-18.52, 0.97) * mm});
            skPoint(sketch, "E33.3.0.8", {"position": v(-15.06, 0.15) * mm});
            skPoint(sketch, "E33.3.0.9", {"position": v(-16.8, 0.56) * mm});
            skPoint(sketch, "E33.3.0.10", {"position": v(-20.25, 1.38) * mm});
            skLineSegment(sketch, "E33.3.0.11", {"start": v(-17.66, 0.77) * mm, "end": v(-17.07, 0.63) * mm});
            skLineSegment(sketch, "E33.3.0.12", {"start": v(-15.06, 0.15) * mm, "end": v(-14.47, 0.01) * mm});
            skPoint(sketch, "E33.3.0.13", {"position": v(-17.21, 0.98) * mm});
            skPoint(sketch, "E33.3.0.14", {"position": v(-13.75, 0.16) * mm});
            skPoint(sketch, "E33.3.0.15", {"position": v(-13.6, -0.2) * mm});
            skPoint(sketch, "E33.3.0.16", {"position": v(-21.12, 1.59) * mm});
            skLineSegment(sketch, "E33.3.0.17", {"start": v(-13.33, -0.26) * mm, "end": v(-12.89, -0.05) * mm});
            skLineSegment(sketch, "E33.3.0.18", {"start": v(-15.93, 0.36) * mm, "end": v(-15.34, 0.22) * mm});
            skPoint(sketch, "E33.3.0.19", {"position": v(-19.22, 1.45) * mm});
            skPoint(sketch, "E33.3.0.20", {"position": v(-15.76, 0.63) * mm});
            skPoint(sketch, "E33.3.0.21", {"position": v(-13.33, -0.26) * mm});
            skPoint(sketch, "E33.3.0.22", {"position": v(-17.49, 1.04) * mm});
            skPoint(sketch, "E33.3.0.23", {"position": v(-18.35, 1.25) * mm});
            skPoint(sketch, "E33.3.0.24", {"position": v(-14.03, 0.22) * mm});
            skLineSegment(sketch, "E33.3.0.25", {"start": v(-18.52, 0.97) * mm, "end": v(-17.93, 0.83) * mm});
            skPoint(sketch, "E33.3.0.26", {"position": v(-14.9, 0.43) * mm});
            skPoint(sketch, "E33.3.0.27", {"position": v(-18.94, 1.39) * mm});
            skPoint(sketch, "E33.3.0.28", {"position": v(-15.48, 0.57) * mm});
            skPoint(sketch, "E33.3.0.29", {"position": v(-18.8, 1.04) * mm});
            skPoint(sketch, "E33.3.0.30", {"position": v(-15.34, 0.22) * mm});
            skLineSegment(sketch, "E33.3.0.31", {"start": v(-13.6, -0.2) * mm, "end": v(-13.16, 0.02) * mm});
            skPoint(sketch, "E33.3.0.32", {"position": v(-11.87, -0.6) * mm});
            skLineSegment(sketch, "E33.3.0.33", {"start": v(-13.33, -0.26) * mm, "end": v(-12.74, -0.4) * mm});
            skPoint(sketch, "E33.3.0.34", {"position": v(-17.07, 0.63) * mm});
            skPoint(sketch, "E33.3.0.35", {"position": v(-19.39, 1.18) * mm});
            skPoint(sketch, "E33.3.0.36", {"position": v(-15.93, 0.36) * mm});
            skLineSegment(sketch, "E33.3.0.37", {"start": v(-19.39, 1.18) * mm, "end": v(-18.8, 1.04) * mm});
            skLineSegment(sketch, "E33.3.0.38", {"start": v(-16.8, 0.56) * mm, "end": v(-16.2, 0.42) * mm});
            skPoint(sketch, "E33.3.0.39", {"position": v(-12.47, -0.46) * mm});
            skLineSegment(sketch, "E33.3.0.40", {"start": v(-20.25, 1.38) * mm, "end": v(-19.66, 1.24) * mm});
            skLineSegment(sketch, "E33.3.0.41", {"start": v(-12.47, -0.46) * mm, "end": v(-11.87, -0.6) * mm});
            skPoint(sketch, "E33.3.0.42", {"position": v(-16.35, 0.77) * mm});
            skPoint(sketch, "E33.3.0.43", {"position": v(-17.93, 0.83) * mm});
            skPoint(sketch, "E33.3.0.44", {"position": v(-18.08, 1.18) * mm});
            skPoint(sketch, "E33.3.0.45", {"position": v(-14.62, 0.36) * mm});
            skPoint(sketch, "E33.3.0.46", {"position": v(-17.66, 0.77) * mm});
            skPoint(sketch, "E33.3.0.47", {"position": v(-14.47, 0.01) * mm});
            skPoint(sketch, "E33.3.0.48", {"position": v(-14.2, -0.05) * mm});
            skPoint(sketch, "E33.3.0.49", {"position": v(-19.8, 1.6) * mm});
            skPoint(sketch, "E33.3.0.50", {"position": v(-20.67, 1.8) * mm});
            skPoint(sketch, "E33.3.0.51", {"position": v(-20.08, 1.66) * mm});
            skLineSegment(sketch, "E33.3.0.52", {"start": v(-15.34, 0.22) * mm, "end": v(-14.9, 0.43) * mm});
            skPoint(sketch, "E33.3.0.53", {"position": v(-11.43, -0.4) * mm});
            skLineSegment(sketch, "E33.3.0.54", {"start": v(-19.39, 1.18) * mm, "end": v(-18.94, 1.39) * mm});
            skLineSegment(sketch, "E33.3.0.55", {"start": v(-18.8, 1.04) * mm, "end": v(-18.35, 1.25) * mm});
            skLineSegment(sketch, "E33.3.0.56", {"start": v(-20.25, 1.38) * mm, "end": v(-19.8, 1.6) * mm});
            skLineSegment(sketch, "E33.3.0.57", {"start": v(-15.06, 0.15) * mm, "end": v(-14.62, 0.36) * mm});
            skLineSegment(sketch, "E33.3.0.58", {"start": v(-17.07, 0.63) * mm, "end": v(-16.62, 0.84) * mm});
            skLineSegment(sketch, "E33.3.0.59", {"start": v(-20.53, 1.45) * mm, "end": v(-20.08, 1.66) * mm});
            skLineSegment(sketch, "E33.3.0.60", {"start": v(-17.93, 0.83) * mm, "end": v(-17.49, 1.04) * mm});
            skLineSegment(sketch, "E33.3.0.61", {"start": v(-16.8, 0.56) * mm, "end": v(-16.35, 0.77) * mm});
            skLineSegment(sketch, "E33.3.0.62", {"start": v(-14.47, 0.01) * mm, "end": v(-14.03, 0.22) * mm});
            skLineSegment(sketch, "E33.3.0.63", {"start": v(-17.66, 0.77) * mm, "end": v(-17.21, 0.98) * mm});
            skLineSegment(sketch, "E33.3.0.64", {"start": v(-18.52, 0.97) * mm, "end": v(-18.08, 1.18) * mm});
            skLineSegment(sketch, "E33.3.0.65", {"start": v(-15.93, 0.36) * mm, "end": v(-15.48, 0.57) * mm});
            skLineSegment(sketch, "E33.3.0.66", {"start": v(-19.66, 1.24) * mm, "end": v(-19.22, 1.45) * mm});
            skLineSegment(sketch, "E33.3.0.67", {"start": v(-14.2, -0.05) * mm, "end": v(-13.75, 0.16) * mm});
            skLineSegment(sketch, "E33.3.0.68", {"start": v(-16.2, 0.42) * mm, "end": v(-15.76, 0.63) * mm});
            skPoint(sketch, "E33.3.0.69", {"position": v(-11.16, -0.46) * mm});
            skLineSegment(sketch, "E33.3.0.70", {"start": v(-21.12, 1.59) * mm, "end": v(-20.53, 1.45) * mm});
            skPoint(sketch, "E33.3.0.71", {"position": v(-13.16, 0.02) * mm});
            skPoint(sketch, "E33.3.0.72", {"position": v(-12.89, -0.05) * mm});
            skLineSegment(sketch, "E33.3.0.73", {"start": v(-12.74, -0.4) * mm, "end": v(-12.3, -0.19) * mm});
            skPoint(sketch, "E33.3.0.74", {"position": v(-12.3, -0.19) * mm});
            skPoint(sketch, "E33.3.0.75", {"position": v(-12.02, -0.25) * mm});
            skLineSegment(sketch, "E33.3.0.76", {"start": v(-12.47, -0.46) * mm, "end": v(-12.02, -0.25) * mm});
            skLineSegment(sketch, "E33.3.0.77", {"start": v(-11.87, -0.6) * mm, "end": v(-11.43, -0.4) * mm});
            skLineSegment(sketch, "E33.3.0.78", {"start": v(-11.6, -0.67) * mm, "end": v(-11.16, -0.46) * mm});
            skLineSegment(sketch, "E33.3.0.79", {"start": v(-11.6, -0.67) * mm, "end": v(-11, -0.8) * mm});
            skLineSegment(sketch, "E33.3.0.80", {"start": v(-11, -0.8) * mm, "end": v(-10.57, -0.6) * mm});
            skLineSegment(sketch, "E33.3.0.81", {"start": v(-10.74, -0.87) * mm, "end": v(-10.3, -0.66) * mm});
            skLineSegment(sketch, "E33.3.0.82", {"start": v(-10.74, -0.87) * mm, "end": v(-10.14, -1) * mm});
            skLineSegment(sketch, "E33.3.0.83", {"start": v(-10.14, -1) * mm, "end": v(-9.7, -0.8) * mm});
            skPoint(sketch, "E33.3.0.84", {"position": v(-10.14, -1) * mm});
            skPoint(sketch, "E33.3.0.85", {"position": v(-10.74, -0.87) * mm});
            skPoint(sketch, "E33.3.0.86", {"position": v(-11, -0.8) * mm});
            skPoint(sketch, "E33.3.0.87", {"position": v(-10.57, -0.6) * mm});
            skPoint(sketch, "E33.3.0.88", {"position": v(-10.3, -0.66) * mm});
            skPoint(sketch, "E33.3.0.89", {"position": v(-9.7, -0.8) * mm});
            skPoint(sketch, "E33.3.0.90", {"position": v(-8.84, -1) * mm});
            skPoint(sketch, "E33.3.0.91", {"position": v(-8.14, -1.48) * mm});
            skLineSegment(sketch, "E33.3.0.92", {"start": v(-9.87, -1.07) * mm, "end": v(-9.43, -0.87) * mm});
            skLineSegment(sketch, "E33.3.0.93", {"start": v(-7.28, -1.69) * mm, "end": v(-6.68, -1.83) * mm});
            skLineSegment(sketch, "E33.3.0.94", {"start": v(-8.41, -1.42) * mm, "end": v(-7.97, -1.21) * mm});
            skLineSegment(sketch, "E33.3.0.95", {"start": v(-8.14, -1.48) * mm, "end": v(-7.55, -1.62) * mm});
            skPoint(sketch, "E33.3.0.96", {"position": v(-6.4, -1.9) * mm});
            skLineSegment(sketch, "E33.3.0.97", {"start": v(-7.55, -1.62) * mm, "end": v(-7.1, -1.42) * mm});
            skPoint(sketch, "E33.3.0.98", {"position": v(-8.56, -1.07) * mm});
            skPoint(sketch, "E33.3.0.99", {"position": v(-7.97, -1.21) * mm});
            skPoint(sketch, "E33.3.0.100", {"position": v(-8.41, -1.42) * mm});
            skPoint(sketch, "E33.3.0.101", {"position": v(-6.68, -1.83) * mm});
            skLineSegment(sketch, "E33.3.0.102", {"start": v(-7.28, -1.69) * mm, "end": v(-6.83, -1.48) * mm});
            skLineSegment(sketch, "E33.3.0.103", {"start": v(-6.4, -1.9) * mm, "end": v(-5.82, -2.03) * mm});
            skLineSegment(sketch, "E33.3.0.104", {"start": v(-9.28, -1.21) * mm, "end": v(-8.84, -1) * mm});
            skLineSegment(sketch, "E33.3.0.105", {"start": v(-6.4, -1.9) * mm, "end": v(-5.97, -1.69) * mm});
            skLineSegment(sketch, "E33.3.0.106", {"start": v(-6.68, -1.83) * mm, "end": v(-6.24, -1.62) * mm});
            skLineSegment(sketch, "E33.3.0.107", {"start": v(-9, -1.28) * mm, "end": v(-8.56, -1.07) * mm});
            skLineSegment(sketch, "E33.3.0.108", {"start": v(-8.14, -1.48) * mm, "end": v(-7.7, -1.28) * mm});
            skPoint(sketch, "E33.3.0.109", {"position": v(-9.43, -0.87) * mm});
            skPoint(sketch, "E33.3.0.110", {"position": v(-7.7, -1.28) * mm});
            skPoint(sketch, "E33.3.0.111", {"position": v(-7.55, -1.62) * mm});
            skPoint(sketch, "E33.3.0.112", {"position": v(-7.28, -1.69) * mm});
            skLineSegment(sketch, "E33.3.0.113", {"start": v(-9, -1.28) * mm, "end": v(-8.41, -1.42) * mm});
            skPoint(sketch, "E33.3.0.114", {"position": v(-9, -1.28) * mm});
            skPoint(sketch, "E33.3.0.115", {"position": v(-9.28, -1.21) * mm});
            skLineSegment(sketch, "E33.3.0.116", {"start": v(-9.87, -1.07) * mm, "end": v(-9.28, -1.21) * mm});
            skPoint(sketch, "E33.3.0.117", {"position": v(-9.87, -1.07) * mm});
            skPoint(sketch, "E33.3.0.118", {"position": v(-7.1, -1.42) * mm});
            skPoint(sketch, "E33.3.0.119", {"position": v(-6.83, -1.48) * mm});
            skPoint(sketch, "E33.3.0.120", {"position": v(-6.24, -1.62) * mm});
            skPoint(sketch, "E33.3.0.121", {"position": v(-5.97, -1.69) * mm});
            skPoint(sketch, "E33.3.0.122", {"position": v(-5.82, -2.03) * mm});
            skPoint(sketch, "E33.3.0.123", {"position": v(-5.38, -1.82) * mm});
            skPoint(sketch, "E33.4.0.0", {"position": v(-17.35, -0.12) * mm});
            skPoint(sketch, "E33.4.0.1", {"position": v(-17.77, 0.3) * mm});
            skLineSegment(sketch, "E33.4.0.2", {"start": v(-15.34, -0.6) * mm, "end": v(-14.75, -0.73) * mm});
            skPoint(sketch, "E33.4.0.3", {"position": v(-20.8, 0.7) * mm});
            skPoint(sketch, "E33.4.0.4", {"position": v(-13.89, -0.94) * mm});
            skPoint(sketch, "E33.4.0.5", {"position": v(-21.67, 0.9) * mm});
            skPoint(sketch, "E33.4.0.6", {"position": v(-12.75, -1.2) * mm});
            skPoint(sketch, "E33.4.0.7", {"position": v(-19.67, 0.43) * mm});
            skPoint(sketch, "E33.4.0.8", {"position": v(-16.2, -0.39) * mm});
            skPoint(sketch, "E33.4.0.9", {"position": v(-17.94, 0.02) * mm});
            skPoint(sketch, "E33.4.0.10", {"position": v(-21.4, 0.84) * mm});
            skLineSegment(sketch, "E33.4.0.11", {"start": v(-18.8, 0.22) * mm, "end": v(-18.21, 0.08) * mm});
            skLineSegment(sketch, "E33.4.0.12", {"start": v(-16.2, -0.39) * mm, "end": v(-15.62, -0.53) * mm});
            skPoint(sketch, "E33.4.0.13", {"position": v(-18.36, 0.43) * mm});
            skPoint(sketch, "E33.4.0.14", {"position": v(-14.9, -0.39) * mm});
            skPoint(sketch, "E33.4.0.15", {"position": v(-14.75, -0.73) * mm});
            skPoint(sketch, "E33.4.0.16", {"position": v(-22.26, 1.04) * mm});
            skLineSegment(sketch, "E33.4.0.17", {"start": v(-14.48, -0.8) * mm, "end": v(-14.04, -0.6) * mm});
            skLineSegment(sketch, "E33.4.0.18", {"start": v(-17.07, -0.18) * mm, "end": v(-16.48, -0.32) * mm});
            skPoint(sketch, "E33.4.0.19", {"position": v(-20.37, 0.9) * mm});
            skPoint(sketch, "E33.4.0.20", {"position": v(-16.9, 0.09) * mm});
            skPoint(sketch, "E33.4.0.21", {"position": v(-14.48, -0.8) * mm});
            skPoint(sketch, "E33.4.0.22", {"position": v(-18.64, 0.5) * mm});
            skPoint(sketch, "E33.4.0.23", {"position": v(-19.5, 0.7) * mm});
            skPoint(sketch, "E33.4.0.24", {"position": v(-15.18, -0.32) * mm});
            skLineSegment(sketch, "E33.4.0.25", {"start": v(-19.67, 0.43) * mm, "end": v(-19.08, 0.29) * mm});
            skPoint(sketch, "E33.4.0.26", {"position": v(-16.04, -0.12) * mm});
            skPoint(sketch, "E33.4.0.27", {"position": v(-20.1, 0.84) * mm});
            skPoint(sketch, "E33.4.0.28", {"position": v(-16.63, 0.02) * mm});
            skPoint(sketch, "E33.4.0.29", {"position": v(-19.94, 0.5) * mm});
            skPoint(sketch, "E33.4.0.30", {"position": v(-16.48, -0.32) * mm});
            skLineSegment(sketch, "E33.4.0.31", {"start": v(-14.75, -0.73) * mm, "end": v(-14.31, -0.53) * mm});
            skPoint(sketch, "E33.4.0.32", {"position": v(-13.02, -1.14) * mm});
            skLineSegment(sketch, "E33.4.0.33", {"start": v(-14.48, -0.8) * mm, "end": v(-13.89, -0.94) * mm});
            skPoint(sketch, "E33.4.0.34", {"position": v(-18.21, 0.08) * mm});
            skPoint(sketch, "E33.4.0.35", {"position": v(-20.53, 0.63) * mm});
            skPoint(sketch, "E33.4.0.36", {"position": v(-17.07, -0.18) * mm});
            skLineSegment(sketch, "E33.4.0.37", {"start": v(-20.53, 0.63) * mm, "end": v(-19.94, 0.5) * mm});
            skLineSegment(sketch, "E33.4.0.38", {"start": v(-17.94, 0.02) * mm, "end": v(-17.35, -0.12) * mm});
            skPoint(sketch, "E33.4.0.39", {"position": v(-13.61, -1) * mm});
            skLineSegment(sketch, "E33.4.0.40", {"start": v(-21.4, 0.84) * mm, "end": v(-20.8, 0.7) * mm});
            skLineSegment(sketch, "E33.4.0.41", {"start": v(-13.61, -1) * mm, "end": v(-13.02, -1.14) * mm});
            skPoint(sketch, "E33.4.0.42", {"position": v(-17.5, 0.23) * mm});
            skPoint(sketch, "E33.4.0.43", {"position": v(-19.08, 0.29) * mm});
            skPoint(sketch, "E33.4.0.44", {"position": v(-19.23, 0.64) * mm});
            skPoint(sketch, "E33.4.0.45", {"position": v(-15.77, -0.18) * mm});
            skPoint(sketch, "E33.4.0.46", {"position": v(-18.8, 0.22) * mm});
            skPoint(sketch, "E33.4.0.47", {"position": v(-15.62, -0.53) * mm});
            skPoint(sketch, "E33.4.0.48", {"position": v(-15.34, -0.6) * mm});
            skPoint(sketch, "E33.4.0.49", {"position": v(-20.96, 1.05) * mm});
            skPoint(sketch, "E33.4.0.50", {"position": v(-21.82, 1.25) * mm});
            skPoint(sketch, "E33.4.0.51", {"position": v(-21.23, 1.11) * mm});
            skPoint(sketch, "E33.4.0.53", {"position": v(-12.58, -0.93) * mm});
            skLineSegment(sketch, "E33.4.0.54", {"start": v(-20.53, 0.63) * mm, "end": v(-20.1, 0.84) * mm});
            skLineSegment(sketch, "E33.4.0.55", {"start": v(-19.94, 0.5) * mm, "end": v(-19.5, 0.7) * mm});
            skLineSegment(sketch, "E33.4.0.56", {"start": v(-21.4, 0.84) * mm, "end": v(-20.96, 1.05) * mm});
            skLineSegment(sketch, "E33.4.0.59", {"start": v(-21.67, 0.9) * mm, "end": v(-21.23, 1.11) * mm});
            skLineSegment(sketch, "E33.4.0.60", {"start": v(-19.08, 0.29) * mm, "end": v(-18.64, 0.5) * mm});
            skLineSegment(sketch, "E33.4.0.62", {"start": v(-15.62, -0.53) * mm, "end": v(-15.18, -0.32) * mm});
            skLineSegment(sketch, "E33.4.0.63", {"start": v(-18.8, 0.22) * mm, "end": v(-18.36, 0.43) * mm});
            skLineSegment(sketch, "E33.4.0.64", {"start": v(-19.67, 0.43) * mm, "end": v(-19.23, 0.64) * mm});
            skLineSegment(sketch, "E33.4.0.66", {"start": v(-20.8, 0.7) * mm, "end": v(-20.37, 0.9) * mm});
            skLineSegment(sketch, "E33.4.0.67", {"start": v(-15.34, -0.6) * mm, "end": v(-14.9, -0.39) * mm});
            skPoint(sketch, "E33.4.0.69", {"position": v(-12.3, -1) * mm});
            skLineSegment(sketch, "E33.4.0.70", {"start": v(-22.26, 1.04) * mm, "end": v(-21.67, 0.9) * mm});
            skPoint(sketch, "E33.4.0.71", {"position": v(-14.31, -0.53) * mm});
            skPoint(sketch, "E33.4.0.72", {"position": v(-14.04, -0.6) * mm});
            skLineSegment(sketch, "E33.4.0.73", {"start": v(-13.89, -0.94) * mm, "end": v(-13.45, -0.73) * mm});
            skPoint(sketch, "E33.4.0.74", {"position": v(-13.45, -0.73) * mm});
            skPoint(sketch, "E33.4.0.75", {"position": v(-13.17, -0.8) * mm});
            skLineSegment(sketch, "E33.4.0.76", {"start": v(-13.61, -1) * mm, "end": v(-13.17, -0.8) * mm});
            skLineSegment(sketch, "E33.4.0.77", {"start": v(-13.02, -1.14) * mm, "end": v(-12.58, -0.93) * mm});
            skLineSegment(sketch, "E33.4.0.78", {"start": v(-12.75, -1.2) * mm, "end": v(-12.3, -1) * mm});
            skLineSegment(sketch, "E33.4.0.79", {"start": v(-12.75, -1.2) * mm, "end": v(-12.16, -1.35) * mm});
            skLineSegment(sketch, "E33.4.0.80", {"start": v(-12.16, -1.35) * mm, "end": v(-11.72, -1.14) * mm});
            skLineSegment(sketch, "E33.4.0.81", {"start": v(-11.88, -1.41) * mm, "end": v(-11.44, -1.2) * mm});
            skLineSegment(sketch, "E33.4.0.82", {"start": v(-11.88, -1.41) * mm, "end": v(-11.3, -1.55) * mm});
            skLineSegment(sketch, "E33.4.0.83", {"start": v(-11.3, -1.55) * mm, "end": v(-10.85, -1.34) * mm});
            skPoint(sketch, "E33.4.0.84", {"position": v(-11.3, -1.55) * mm});
            skPoint(sketch, "E33.4.0.85", {"position": v(-11.88, -1.41) * mm});
            skPoint(sketch, "E33.4.0.86", {"position": v(-12.16, -1.35) * mm});
            skPoint(sketch, "E33.4.0.87", {"position": v(-11.72, -1.14) * mm});
            skPoint(sketch, "E33.4.0.88", {"position": v(-11.44, -1.2) * mm});
            skPoint(sketch, "E33.4.0.89", {"position": v(-10.85, -1.34) * mm});
            skPoint(sketch, "E33.4.0.90", {"position": v(-9.99, -1.55) * mm});
            skPoint(sketch, "E33.4.0.91", {"position": v(-9.29, -2.03) * mm});
            skLineSegment(sketch, "E33.4.0.92", {"start": v(-11.02, -1.62) * mm, "end": v(-10.58, -1.4) * mm});
            skLineSegment(sketch, "E33.4.0.93", {"start": v(-8.42, -2.23) * mm, "end": v(-7.83, -2.37) * mm});
            skLineSegment(sketch, "E33.4.0.94", {"start": v(-9.56, -1.96) * mm, "end": v(-9.12, -1.75) * mm});
            skLineSegment(sketch, "E33.4.0.95", {"start": v(-9.29, -2.03) * mm, "end": v(-8.7, -2.17) * mm});
            skPoint(sketch, "E33.4.0.96", {"position": v(-7.56, -2.44) * mm});
            skLineSegment(sketch, "E33.4.0.97", {"start": v(-8.7, -2.17) * mm, "end": v(-8.26, -1.96) * mm});
            skPoint(sketch, "E33.4.0.98", {"position": v(-9.71, -1.61) * mm});
            skPoint(sketch, "E33.4.0.99", {"position": v(-9.12, -1.75) * mm});
            skPoint(sketch, "E33.4.0.100", {"position": v(-9.56, -1.96) * mm});
            skPoint(sketch, "E33.4.0.101", {"position": v(-7.83, -2.37) * mm});
            skLineSegment(sketch, "E33.4.0.102", {"start": v(-8.42, -2.23) * mm, "end": v(-7.98, -2.02) * mm});
            skLineSegment(sketch, "E33.4.0.103", {"start": v(-7.56, -2.44) * mm, "end": v(-6.97, -2.58) * mm});
            skLineSegment(sketch, "E33.4.0.104", {"start": v(-10.43, -1.76) * mm, "end": v(-9.99, -1.55) * mm});
            skLineSegment(sketch, "E33.4.0.105", {"start": v(-7.56, -2.44) * mm, "end": v(-7.12, -2.23) * mm});
            skLineSegment(sketch, "E33.4.0.106", {"start": v(-7.83, -2.37) * mm, "end": v(-7.4, -2.16) * mm});
            skLineSegment(sketch, "E33.4.0.107", {"start": v(-10.15, -1.82) * mm, "end": v(-9.71, -1.61) * mm});
            skLineSegment(sketch, "E33.4.0.108", {"start": v(-9.29, -2.03) * mm, "end": v(-8.85, -1.82) * mm});
            skPoint(sketch, "E33.4.0.109", {"position": v(-10.58, -1.4) * mm});
            skPoint(sketch, "E33.4.0.110", {"position": v(-8.85, -1.82) * mm});
            skPoint(sketch, "E33.4.0.111", {"position": v(-8.7, -2.17) * mm});
            skPoint(sketch, "E33.4.0.112", {"position": v(-8.42, -2.23) * mm});
            skLineSegment(sketch, "E33.4.0.113", {"start": v(-10.15, -1.82) * mm, "end": v(-9.56, -1.96) * mm});
            skPoint(sketch, "E33.4.0.114", {"position": v(-10.15, -1.82) * mm});
            skPoint(sketch, "E33.4.0.115", {"position": v(-10.43, -1.76) * mm});
            skLineSegment(sketch, "E33.4.0.116", {"start": v(-11.02, -1.62) * mm, "end": v(-10.43, -1.76) * mm});
            skPoint(sketch, "E33.4.0.117", {"position": v(-11.02, -1.62) * mm});
            skPoint(sketch, "E33.4.0.118", {"position": v(-8.26, -1.96) * mm});
            skPoint(sketch, "E33.4.0.119", {"position": v(-7.98, -2.02) * mm});
            skPoint(sketch, "E33.4.0.120", {"position": v(-7.4, -2.16) * mm});
            skPoint(sketch, "E33.4.0.121", {"position": v(-7.12, -2.23) * mm});
            skPoint(sketch, "E33.4.0.122", {"position": v(-6.97, -2.58) * mm});
            skPoint(sketch, "E33.4.0.123", {"position": v(-6.53, -2.37) * mm});
            skLineSegment(sketch, "E33.direction1", {"start": v(-17.67, 3.22) * mm, "end": v(-18.38, 2.88) * mm, "construction": true});
            skLineSegment(sketch, "E34", {"start": v(-18.38, 2.88) * mm, "end": v(-15.2, 2.13) * mm});
            skLineSegment(sketch, "E35", {"start": v(-3.08, -0.74) * mm, "end": v(-3.67, -0.6) * mm});
            skLineSegment(sketch, "E36.trimOffspring", {"start": v(-4.54, -0.4) * mm, "end": v(-3.95, -0.53) * mm});
            skLineSegment(sketch, "E37.trimOffspring", {"start": v(-5.4, -0.19) * mm, "end": v(-4.81, -0.33) * mm});
            skLineSegment(sketch, "E38.trimOffspring", {"start": v(-6.27, 0.02) * mm, "end": v(-5.68, -0.12) * mm});
            skLineSegment(sketch, "E39.trimOffspring", {"start": v(-7.13, 0.22) * mm, "end": v(-6.54, 0.08) * mm});
            skLineSegment(sketch, "E40.trimOffspring", {"start": v(-8, 0.43) * mm, "end": v(-7.4, 0.29) * mm});
            skLineSegment(sketch, "E41.trimOffspring", {"start": v(-8.86, 0.63) * mm, "end": v(-8.27, 0.5) * mm});
            skLineSegment(sketch, "E42.trimOffspring", {"start": v(-9.73, 0.84) * mm, "end": v(-9.14, 0.7) * mm});
            skLineSegment(sketch, "E43.trimOffspring", {"start": v(-10.6, 1.04) * mm, "end": v(-10, 0.9) * mm});
            skLineSegment(sketch, "E44", {"start": v(-9.15, -0.12) * mm, "end": v(-8.56, -0.26) * mm});
            skLineSegment(sketch, "E45", {"start": v(-8.28, -0.32) * mm, "end": v(-7.7, -0.46) * mm});
            skLineSegment(sketch, "E46", {"start": v(-7.42, -0.53) * mm, "end": v(-6.83, -0.67) * mm});
            skLineSegment(sketch, "E47", {"start": v(-6.55, -0.73) * mm, "end": v(-5.96, -0.87) * mm});
            skLineSegment(sketch, "E48", {"start": v(-5.69, -0.94) * mm, "end": v(-5.1, -1.08) * mm});
            skLineSegment(sketch, "E49", {"start": v(-4.82, -1.14) * mm, "end": v(-4.23, -1.28) * mm});
            skLineSegment(sketch, "E50", {"start": v(-5.38, -1.82) * mm, "end": v(-5.97, -1.69) * mm});
            skLineSegment(sketch, "E51", {"start": v(-6.53, -2.37) * mm, "end": v(-7.12, -2.23) * mm});
            skLineSegment(sketch, "E52", {"start": v(-7.4, -2.16) * mm, "end": v(-7.98, -2.02) * mm});
            skLineSegment(sketch, "E53", {"start": v(-8.26, -1.96) * mm, "end": v(-8.85, -1.82) * mm});
            skLineSegment(sketch, "E54", {"start": v(-9.71, -1.61) * mm, "end": v(-9.12, -1.75) * mm});
            skLineSegment(sketch, "E55", {"start": v(-9.99, -1.55) * mm, "end": v(-10.58, -1.4) * mm});
            skLineSegment(sketch, "E56", {"start": v(-10.85, -1.34) * mm, "end": v(-11.44, -1.2) * mm});
            skLineSegment(sketch, "E57", {"start": v(-12.3, -1) * mm, "end": v(-11.72, -1.14) * mm});
            skLineSegment(sketch, "E58", {"start": v(-15.18, -0.32) * mm, "end": v(-18.36, 0.43) * mm});
            skLineSegment(sketch, "E59", {"start": v(-18.21, 0.08) * mm, "end": v(-17.07, -0.18) * mm});
            skLineSegment(sketch, "E60.trimOffspring", {"start": v(-16.48, -0.32) * mm, "end": v(-16.2, -0.39) * mm});
            skLineSegment(sketch, "E61", {"start": v(-23, 0.7) * mm, "end": v(-19.1, -0.23) * mm});
            skLineSegment(sketch, "E62.trimOffspring", {"start": v(-11.46, 1.24) * mm, "end": v(-10.87, 1.1) * mm});
            skLineSegment(sketch, "E63.trimOffspring", {"start": v(-12.32, 1.45) * mm, "end": v(-11.73, 1.3) * mm});
            skLineSegment(sketch, "E64.trimOffspring", {"start": v(-13.19, 1.65) * mm, "end": v(-12.6, 1.51) * mm});
            skLineSegment(sketch, "E65.trimOffspring", {"start": v(-14.05, 1.86) * mm, "end": v(-13.46, 1.72) * mm});
            skLineSegment(sketch, "E66.trimOffspring", {"start": v(-14.92, 2.06) * mm, "end": v(-14.33, 1.92) * mm});
            skLineSegment(sketch, "E67", {"start": v(-14.34, 1.11) * mm, "end": v(-13.75, 0.97) * mm});
            skLineSegment(sketch, "E68", {"start": v(-13.47, 0.9) * mm, "end": v(-12.88, 0.77) * mm});
            skLineSegment(sketch, "E69", {"start": v(-14.9, -0.39) * mm, "end": v(-14.31, -0.53) * mm});
            skLineSegment(sketch, "E70", {"start": v(-14.04, -0.6) * mm, "end": v(-13.45, -0.73) * mm});
            skLineSegment(sketch, "E71", {"start": v(-13.17, -0.8) * mm, "end": v(-12.58, -0.93) * mm});
            skLineSegment(sketch, "E72", {"start": v(-12.02, -0.25) * mm, "end": v(-11.43, -0.4) * mm});
            skLineSegment(sketch, "E73", {"start": v(-11.16, -0.46) * mm, "end": v(-10.57, -0.6) * mm});
            skLineSegment(sketch, "E74", {"start": v(-10.3, -0.66) * mm, "end": v(-9.7, -0.8) * mm});
            skLineSegment(sketch, "E75", {"start": v(-9.43, -0.87) * mm, "end": v(-8.84, -1) * mm});
            skLineSegment(sketch, "E76", {"start": v(-8.56, -1.07) * mm, "end": v(-7.97, -1.21) * mm});
            skLineSegment(sketch, "E77", {"start": v(-7.7, -1.28) * mm, "end": v(-7.1, -1.42) * mm});
            skLineSegment(sketch, "E78", {"start": v(-6.83, -1.48) * mm, "end": v(-6.24, -1.62) * mm});
            skLineSegment(sketch, "E79", {"start": v(-9.42, -0.05) * mm, "end": v(-10.01, 0.09) * mm});
            skLineSegment(sketch, "E80", {"start": v(-10.29, 0.15) * mm, "end": v(-10.88, 0.3) * mm});
            skLineSegment(sketch, "E81", {"start": v(-11.15, 0.36) * mm, "end": v(-11.74, 0.5) * mm});
            skLineSegment(sketch, "E82", {"start": v(-12.02, 0.56) * mm, "end": v(-12.6, 0.7) * mm});
            skLineSegment(sketch, "E83", {"start": v(-14.61, 1.18) * mm, "end": v(-15.2, 1.32) * mm});
            skLineSegment(sketch, "E84", {"start": v(-15.48, 1.38) * mm, "end": v(-16.07, 1.52) * mm});
            skLineSegment(sketch, "E85", {"start": v(-15.76, 0.63) * mm, "end": v(-16.35, 0.77) * mm});
            skLineSegment(sketch, "E86", {"start": v(-14.9, 0.43) * mm, "end": v(-15.48, 0.57) * mm});
            skLineSegment(sketch, "E87", {"start": v(-14.03, 0.22) * mm, "end": v(-14.62, 0.36) * mm});
            skLineSegment(sketch, "E88", {"start": v(-13.16, 0.02) * mm, "end": v(-13.75, 0.16) * mm});
            skLineSegment(sketch, "E89", {"start": v(-12.3, -0.19) * mm, "end": v(-12.89, -0.05) * mm});
            skLineSegment(sketch, "E90", {"start": v(-18.94, 2.2) * mm, "end": v(-19.53, 2.34) * mm});
            skLineSegment(sketch, "E91", {"start": v(-18.66, 2.13) * mm, "end": v(-18.07, 2) * mm});
            skLineSegment(sketch, "E92", {"start": v(-17.8, 1.93) * mm, "end": v(-17.2, 1.8) * mm});
            skLineSegment(sketch, "E93", {"start": v(-16.93, 1.73) * mm, "end": v(-16.34, 1.59) * mm});
            skLineSegment(sketch, "E94", {"start": v(-17.21, 0.98) * mm, "end": v(-16.62, 0.84) * mm});
            skLineSegment(sketch, "E95", {"start": v(-17.49, 1.04) * mm, "end": v(-18.08, 1.18) * mm});
            skLineSegment(sketch, "E96", {"start": v(-18.35, 1.25) * mm, "end": v(-18.94, 1.39) * mm});
            skLineSegment(sketch, "E97", {"start": v(-19.22, 1.45) * mm, "end": v(-19.8, 1.6) * mm});
            skLineSegment(sketch, "E98", {"start": v(-20.08, 1.66) * mm, "end": v(-20.67, 1.8) * mm});
            skLineSegment(sketch, "E99", {"start": v(-19.5, 0.7) * mm, "end": v(-20.1, 0.84) * mm});
            skLineSegment(sketch, "E100", {"start": v(-18.64, 0.5) * mm, "end": v(-19.23, 0.64) * mm});
            skLineSegment(sketch, "E101", {"start": v(-20.37, 0.9) * mm, "end": v(-20.96, 1.05) * mm});
            skLineSegment(sketch, "E102", {"start": v(-21.23, 1.11) * mm, "end": v(-21.82, 1.25) * mm});
            skLineSegment(sketch, "E103", {"start": v(-21.88, -1.83) * mm, "end": v(-21.24, -1.52) * mm});
            skPoint(sketch, "E104.endSnap0", {"position": v(-15.34, -1.12) * mm});
            skLineSegment(sketch, "E105", {"start": v(-15.58, -1.23) * mm, "end": v(-17.86, -2.31) * mm});
            skLineSegment(sketch, "E106", {"start": v(-21.13, -1.47) * mm, "end": v(-17.97, -2.36) * mm, "construction": true});
            skLineSegment(sketch, "E107", {"start": v(-19.55, -1.92) * mm, "end": v(-20.3, -2.27) * mm, "construction": true});
            skLineSegment(sketch, "E108", {"start": v(-21.01, -1.42) * mm, "end": v(-17.86, -2.31) * mm});
            skLineSegment(sketch, "E109", {"start": v(-21.24, -1.52) * mm, "end": v(-19.79, -1.94) * mm});
            skLineSegment(sketch, "E110", {"start": v(-19.79, -1.94) * mm, "end": v(-20.42, -2.24) * mm});
            skLineSegment(sketch, "E111", {"start": v(-20.18, -2.3) * mm, "end": v(-19.54, -2) * mm});
            skLineSegment(sketch, "E112", {"start": v(-19.54, -2) * mm, "end": v(-18.09, -2.42) * mm});
            skLineSegment(sketch, "E113", {"start": v(-18.94, -0.43) * mm, "end": v(-15.58, -1.23) * mm});
            skLineSegment(sketch, "E114.trimOffspring", {"start": v(-18.09, -2.42) * mm, "end": v(-18.72, -2.72) * mm});
            skLineSegment(sketch, "E115.trimOffspring", {"start": v(-20.18, -2.3) * mm, "end": v(-18.72, -2.72) * mm});
            skLineSegment(sketch, "E116.trimOffspring", {"start": v(-21.01, -1.42) * mm, "end": v(-18.94, -0.43) * mm});
            skLineSegment(sketch, "E117.0", {"start": v(2.16, 11.89) * mm, "end": v(-13.9, 15.7) * mm});
            skLineSegment(sketch, "E117.1", {"start": v(-0.47, 0.76) * mm, "end": v(2.16, 11.89) * mm});
            skLineSegment(sketch, "E117.2", {"start": v(-16.54, 4.57) * mm, "end": v(-0.47, 0.76) * mm});
            skLineSegment(sketch, "E117.3", {"start": v(-13.9, 15.7) * mm, "end": v(-16.54, 4.57) * mm});
            skLineSegment(sketch, "E118", {"start": v(-19.1, -0.23) * mm, "end": v(-22.6, -1.89) * mm});
            skLineSegment(sketch, "E119", {"start": v(-22.6, -1.89) * mm, "end": v(-18.7, -3) * mm});
            skLineSegment(sketch, "E120", {"start": v(-18.7, -3) * mm, "end": v(-14.94, -1.21) * mm});
            skLineSegment(sketch, "E121.trimOffspring", {"start": v(-14.94, -1.21) * mm, "end": v(-7.68, -2.93) * mm});
            skPoint(sketch, "E104.end.orphan", {"position": v(-15.34, -1.12) * mm});
            skLineSegment(sketch, "E122.trimOffspring", {"start": v(-22.26, 1.04) * mm, "end": v(-23, 0.7) * mm});
            skLineSegment(sketch, "E123.trimOffspring", {"start": v(-21.12, 1.59) * mm, "end": v(-21.82, 1.25) * mm});
            skLineSegment(sketch, "E124.trimOffspring", {"start": v(-19.97, 2.13) * mm, "end": v(-20.67, 1.8) * mm});
            skLineSegment(sketch, "E125", {"start": v(-6.97, -2.58) * mm, "end": v(-6.94, -2.58) * mm});
            skLineSegment(sketch, "E126", {"start": v(-6.53, -2.37) * mm, "end": v(-6.5, -2.37) * mm});
            skLineSegment(sketch, "E127", {"start": v(-5.82, -2.03) * mm, "end": v(-5.8, -2.04) * mm});
            skLineSegment(sketch, "E128.trimOffspring", {"start": v(-6.5, -2.37) * mm, "end": v(-5.8, -2.04) * mm});
            skLineSegment(sketch, "E129", {"start": v(-5.38, -1.82) * mm, "end": v(-5.35, -1.83) * mm});
            skLineSegment(sketch, "E130", {"start": v(-4.67, -1.5) * mm, "end": v(-4.65, -1.5) * mm});
            skLineSegment(sketch, "E131", {"start": v(-4.23, -1.28) * mm, "end": v(-4.2, -1.29) * mm});
            skLineSegment(sketch, "E132.trimOffspring", {"start": v(-5.35, -1.83) * mm, "end": v(-4.65, -1.5) * mm});
            skLineSegment(sketch, "E133.trimOffspring", {"start": v(-4.2, -1.29) * mm, "end": v(-3.5, -0.95) * mm});
            skLineSegment(sketch, "E134", {"start": v(-3.52, -0.95) * mm, "end": v(-3.5, -0.95) * mm});
            skLineSegment(sketch, "E135", {"start": v(-3.08, -0.74) * mm, "end": v(-3.06, -0.74) * mm});
            skLineSegment(sketch, "E136.trimOffspring", {"start": v(-3.06, -0.74) * mm, "end": v(-2.35, -0.4) * mm});
            skLineSegment(sketch, "E137.trimOffspring", {"start": v(-1.93, -0.2) * mm, "end": v(-1.9, -0.2) * mm});
            skLineSegment(sketch, "E138.trimOffspring", {"start": v(-2.8, 0.01) * mm, "end": v(-2.52, -0.05) * mm});
            skLineSegment(sketch, "E139.trimOffspring", {"start": v(-3.66, 0.21) * mm, "end": v(-3.39, 0.15) * mm});
            skLineSegment(sketch, "E140.trimOffspring", {"start": v(-4.53, 0.42) * mm, "end": v(-4.26, 0.35) * mm});
            skLineSegment(sketch, "E141.trimOffspring", {"start": v(-5.4, 0.62) * mm, "end": v(-5.12, 0.56) * mm});
            skLineSegment(sketch, "E142.trimOffspring", {"start": v(-6.26, 0.83) * mm, "end": v(-5.99, 0.76) * mm});
            skLineSegment(sketch, "E143.trimOffspring", {"start": v(-7.12, 1.03) * mm, "end": v(-6.85, 0.97) * mm});
            skLineSegment(sketch, "E144.trimOffspring", {"start": v(-7.99, 1.24) * mm, "end": v(-7.72, 1.17) * mm});
            skLineSegment(sketch, "E145.trimOffspring", {"start": v(-8.85, 1.44) * mm, "end": v(-8.58, 1.38) * mm});
            skLineSegment(sketch, "E146.trimOffspring", {"start": v(-9.72, 1.65) * mm, "end": v(-9.45, 1.58) * mm});
            skLineSegment(sketch, "E147.trimOffspring", {"start": v(-10.58, 1.85) * mm, "end": v(-10.31, 1.79) * mm});
            skLineSegment(sketch, "E148.trimOffspring", {"start": v(-11.45, 2.06) * mm, "end": v(-11.18, 2) * mm});
            skLineSegment(sketch, "E149.trimOffspring", {"start": v(-12.32, 2.26) * mm, "end": v(-12.04, 2.2) * mm});
            skLineSegment(sketch, "E150.trimOffspring", {"start": v(-13.18, 2.47) * mm, "end": v(-12.9, 2.4) * mm});
            skLineSegment(sketch, "E151.trimOffspring", {"start": v(-14.05, 2.67) * mm, "end": v(-13.77, 2.6) * mm});
            skLineSegment(sketch, "E152.trimOffspring", {"start": v(-14.91, 2.88) * mm, "end": v(-14.64, 2.81) * mm});
            skLineSegment(sketch, "E153.trimOffspring", {"start": v(-15.78, 3.08) * mm, "end": v(-15.5, 3.02) * mm});
            skLineSegment(sketch, "E154.trimOffspring", {"start": v(-18.82, 2.67) * mm, "end": v(-19.53, 2.34) * mm});
            skSolve(sketch);
        }
        {
            var Q0;
            Q0=qCreatedBy(makeId("Top.planeOp"),FACE);
            var sketch = newSketch(context, id + "F1", { "sketchPlane" : qUnion([Q0])});
            skLineSegment(sketch, "E155.bottom", {"start": v(-38.1, 38.1) * mm, "end": v(38.1, 38.1) * mm});
            skLineSegment(sketch, "E155.top", {"start": v(-38.1, -38.1) * mm, "end": v(38.1, -38.1) * mm});
            skLineSegment(sketch, "E155.left", {"start": v(-38.1, 38.1) * mm, "end": v(-38.1, -38.1) * mm});
            skLineSegment(sketch, "E155.right", {"start": v(38.1, 38.1) * mm, "end": v(38.1, -38.1) * mm});
            skPoint(sketch, "E155.middle", {"position": v(0, 0) * mm});
            skSolve(sketch);
        }
        {
            var Q0;
            Q0 = qSketchRegion(id + "F1", true);
            extrude(context, id + "F2", {"entities" : qUnion([Q0]), "oppositeDirection" : true, "depth" : 76.2 * mm, "offsetDistance" : 25.4 * mm});
        }
        {
            var Q0;
            Q0=makeQuery(id+"F0.imprint","IMPRINT",FACE,{"disambiguationData":[TD([[makeQuery(id+"F0.imprint","IMPRINT",EDGE,{"derivedFrom":sQuery(id+"F0.wireOp",EDGE,"E0")}),1.0]])]});
            var Q1;
            Q1=makeQuery(id+"F0.imprint","IMPRINT",FACE,{"disambiguationData":[TD([[makeQuery(id+"F0.imprint","IMPRINT",EDGE,{"derivedFrom":sQuery(id+"F0.wireOp",EDGE,"E1")}),1.0]])]});
            var Q2;
            Q2=makeQuery(id+"F0.imprint","IMPRINT",FACE,{"disambiguationData":[TD([[makeQuery(id+"F0.imprint","IMPRINT",EDGE,{"derivedFrom":sQuery(id+"F0.wireOp",EDGE,"E33.1.0.40")}),1.0]])]});
            var Q3;
            Q3=makeQuery(id+"F0.imprint","IMPRINT",FACE,{"disambiguationData":[TD([[makeQuery(id+"F0.imprint","IMPRINT",EDGE,{"derivedFrom":sQuery(id+"F0.wireOp",EDGE,"E33.1.0.37")}),1.0]])]});
            var Q4;
            Q4=makeQuery(id+"F0.imprint","IMPRINT",FACE,{"disambiguationData":[TD([[makeQuery(id+"F0.imprint","IMPRINT",EDGE,{"derivedFrom":sQuery(id+"F0.wireOp",EDGE,"E33.1.0.25")}),1.0]])]});
            var Q5;
            Q5=makeQuery(id+"F0.imprint","IMPRINT",FACE,{"disambiguationData":[TD([[makeQuery(id+"F0.imprint","IMPRINT",EDGE,{"derivedFrom":sQuery(id+"F0.wireOp",EDGE,"E33.1.0.11")}),1.0]])]});
            var Q6;
            Q6=makeQuery(id+"F0.imprint","IMPRINT",FACE,{"disambiguationData":[TD([[makeQuery(id+"F0.imprint","IMPRINT",EDGE,{"derivedFrom":sQuery(id+"F0.wireOp",EDGE,"E33.1.0.38")}),1.0]])]});
            var Q7;
            Q7=makeQuery(id+"F0.imprint","IMPRINT",FACE,{"disambiguationData":[TD([[makeQuery(id+"F0.imprint","IMPRINT",EDGE,{"derivedFrom":sQuery(id+"F0.wireOp",EDGE,"E33.1.0.18")}),1.0]])]});
            var Q8;
            Q8=makeQuery(id+"F0.imprint","IMPRINT",FACE,{"disambiguationData":[TD([[makeQuery(id+"F0.imprint","IMPRINT",EDGE,{"derivedFrom":sQuery(id+"F0.wireOp",EDGE,"E33.1.0.12")}),1.0]])]});
            var Q9;
            Q9=makeQuery(id+"F0.imprint","IMPRINT",FACE,{"disambiguationData":[TD([[makeQuery(id+"F0.imprint","IMPRINT",EDGE,{"derivedFrom":sQuery(id+"F0.wireOp",EDGE,"E33.1.0.2")}),1.0]])]});
            var Q10;
            Q10=makeQuery(id+"F0.imprint","IMPRINT",FACE,{"disambiguationData":[TD([[makeQuery(id+"F0.imprint","IMPRINT",EDGE,{"derivedFrom":sQuery(id+"F0.wireOp",EDGE,"E33.1.0.17")}),-1.0]])]});
            var Q11;
            Q11=makeQuery(id+"F0.imprint","IMPRINT",FACE,{"disambiguationData":[TD([[makeQuery(id+"F0.imprint","IMPRINT",EDGE,{"derivedFrom":sQuery(id+"F0.wireOp",EDGE,"E33.1.0.41")}),1.0]])]});
            var Q12;
            Q12=makeQuery(id+"F0.imprint","IMPRINT",FACE,{"disambiguationData":[TD([[makeQuery(id+"F0.imprint","IMPRINT",EDGE,{"derivedFrom":sQuery(id+"F0.wireOp",EDGE,"E33.1.0.78")}),-1.0]])]});
            var Q13;
            Q13=makeQuery(id+"F0.imprint","IMPRINT",FACE,{"disambiguationData":[TD([[makeQuery(id+"F0.imprint","IMPRINT",EDGE,{"derivedFrom":sQuery(id+"F0.wireOp",EDGE,"E33.1.0.81")}),-1.0]])]});
            var Q14;
            Q14=makeQuery(id+"F0.imprint","IMPRINT",FACE,{"disambiguationData":[TD([[makeQuery(id+"F0.imprint","IMPRINT",EDGE,{"derivedFrom":sQuery(id+"F0.wireOp",EDGE,"E33.1.0.92")}),-1.0]])]});
            var Q15;
            Q15=makeQuery(id+"F0.imprint","IMPRINT",FACE,{"disambiguationData":[TD([[makeQuery(id+"F0.imprint","IMPRINT",EDGE,{"derivedFrom":sQuery(id+"F0.wireOp",EDGE,"E33.1.0.94")}),1.0]])]});
            var Q16;
            Q16=makeQuery(id+"F0.imprint","IMPRINT",FACE,{"disambiguationData":[TD([[makeQuery(id+"F0.imprint","IMPRINT",EDGE,{"derivedFrom":sQuery(id+"F0.wireOp",EDGE,"E33.1.0.95")}),1.0]])]});
            var Q17;
            Q17=makeQuery(id+"F0.imprint","IMPRINT",FACE,{"disambiguationData":[TD([[makeQuery(id+"F0.imprint","IMPRINT",EDGE,{"derivedFrom":sQuery(id+"F0.wireOp",EDGE,"E33.1.0.93")}),1.0]])]});
            var Q18;
            Q18=makeQuery(id+"F0.imprint","IMPRINT",FACE,{"disambiguationData":[TD([[makeQuery(id+"F0.imprint","IMPRINT",EDGE,{"derivedFrom":sQuery(id+"F0.wireOp",EDGE,"E33.2.0.93")}),1.0]])]});
            var Q19;
            Q19=makeQuery(id+"F0.imprint","IMPRINT",FACE,{"disambiguationData":[TD([[makeQuery(id+"F0.imprint","IMPRINT",EDGE,{"derivedFrom":sQuery(id+"F0.wireOp",EDGE,"E33.2.0.95")}),1.0]])]});
            var Q20;
            Q20=makeQuery(id+"F0.imprint","IMPRINT",FACE,{"disambiguationData":[TD([[makeQuery(id+"F0.imprint","IMPRINT",EDGE,{"derivedFrom":sQuery(id+"F0.wireOp",EDGE,"E33.2.0.94")}),1.0]])]});
            var Q21;
            Q21=makeQuery(id+"F0.imprint","IMPRINT",FACE,{"disambiguationData":[TD([[makeQuery(id+"F0.imprint","IMPRINT",EDGE,{"derivedFrom":sQuery(id+"F0.wireOp",EDGE,"E33.2.0.92")}),-1.0]])]});
            var Q22;
            Q22=makeQuery(id+"F0.imprint","IMPRINT",FACE,{"disambiguationData":[TD([[makeQuery(id+"F0.imprint","IMPRINT",EDGE,{"derivedFrom":sQuery(id+"F0.wireOp",EDGE,"E33.2.0.81")}),-1.0]])]});
            var Q23;
            Q23=makeQuery(id+"F0.imprint","IMPRINT",FACE,{"disambiguationData":[TD([[makeQuery(id+"F0.imprint","IMPRINT",EDGE,{"derivedFrom":sQuery(id+"F0.wireOp",EDGE,"E33.2.0.78")}),-1.0]])]});
            var Q24;
            Q24=makeQuery(id+"F0.imprint","IMPRINT",FACE,{"disambiguationData":[TD([[makeQuery(id+"F0.imprint","IMPRINT",EDGE,{"derivedFrom":sQuery(id+"F0.wireOp",EDGE,"E33.2.0.41")}),1.0]])]});
            var Q25;
            Q25=makeQuery(id+"F0.imprint","IMPRINT",FACE,{"disambiguationData":[TD([[makeQuery(id+"F0.imprint","IMPRINT",EDGE,{"derivedFrom":sQuery(id+"F0.wireOp",EDGE,"E33.2.0.17")}),-1.0]])]});
            var Q26;
            Q26=makeQuery(id+"F0.imprint","IMPRINT",FACE,{"disambiguationData":[TD([[makeQuery(id+"F0.imprint","IMPRINT",EDGE,{"derivedFrom":sQuery(id+"F0.wireOp",EDGE,"E33.2.0.2")}),1.0]])]});
            var Q27;
            Q27=makeQuery(id+"F0.imprint","IMPRINT",FACE,{"disambiguationData":[TD([[makeQuery(id+"F0.imprint","IMPRINT",EDGE,{"derivedFrom":sQuery(id+"F0.wireOp",EDGE,"E33.2.0.12")}),1.0]])]});
            var Q28;
            Q28=makeQuery(id+"F0.imprint","IMPRINT",FACE,{"disambiguationData":[TD([[makeQuery(id+"F0.imprint","IMPRINT",EDGE,{"derivedFrom":sQuery(id+"F0.wireOp",EDGE,"E33.2.0.18")}),1.0]])]});
            var Q29;
            Q29=makeQuery(id+"F0.imprint","IMPRINT",FACE,{"disambiguationData":[TD([[makeQuery(id+"F0.imprint","IMPRINT",EDGE,{"derivedFrom":sQuery(id+"F0.wireOp",EDGE,"E33.2.0.38")}),1.0]])]});
            var Q30;
            Q30=makeQuery(id+"F0.imprint","IMPRINT",FACE,{"disambiguationData":[TD([[makeQuery(id+"F0.imprint","IMPRINT",EDGE,{"derivedFrom":sQuery(id+"F0.wireOp",EDGE,"E33.2.0.11")}),1.0]])]});
            var Q31;
            Q31=makeQuery(id+"F0.imprint","IMPRINT",FACE,{"disambiguationData":[TD([[makeQuery(id+"F0.imprint","IMPRINT",EDGE,{"derivedFrom":sQuery(id+"F0.wireOp",EDGE,"E33.2.0.25")}),1.0]])]});
            var Q32;
            Q32=makeQuery(id+"F0.imprint","IMPRINT",FACE,{"disambiguationData":[TD([[makeQuery(id+"F0.imprint","IMPRINT",EDGE,{"derivedFrom":sQuery(id+"F0.wireOp",EDGE,"E33.2.0.37")}),1.0]])]});
            var Q33;
            Q33=makeQuery(id+"F0.imprint","IMPRINT",FACE,{"disambiguationData":[TD([[makeQuery(id+"F0.imprint","IMPRINT",EDGE,{"derivedFrom":sQuery(id+"F0.wireOp",EDGE,"E33.2.0.40")}),1.0]])]});
            var Q34;
            Q34=makeQuery(id+"F0.imprint","IMPRINT",FACE,{"disambiguationData":[TD([[makeQuery(id+"F0.imprint","IMPRINT",EDGE,{"derivedFrom":sQuery(id+"F0.wireOp",EDGE,"E33.3.0.40")}),1.0]])]});
            var Q35;
            Q35=makeQuery(id+"F0.imprint","IMPRINT",FACE,{"disambiguationData":[TD([[makeQuery(id+"F0.imprint","IMPRINT",EDGE,{"derivedFrom":sQuery(id+"F0.wireOp",EDGE,"E33.3.0.37")}),1.0]])]});
            var Q36;
            Q36=makeQuery(id+"F0.imprint","IMPRINT",FACE,{"disambiguationData":[TD([[makeQuery(id+"F0.imprint","IMPRINT",EDGE,{"derivedFrom":sQuery(id+"F0.wireOp",EDGE,"E33.3.0.25")}),1.0]])]});
            var Q37;
            Q37=makeQuery(id+"F0.imprint","IMPRINT",FACE,{"disambiguationData":[TD([[makeQuery(id+"F0.imprint","IMPRINT",EDGE,{"derivedFrom":sQuery(id+"F0.wireOp",EDGE,"E33.3.0.11")}),1.0]])]});
            var Q38;
            Q38=makeQuery(id+"F0.imprint","IMPRINT",FACE,{"disambiguationData":[TD([[makeQuery(id+"F0.imprint","IMPRINT",EDGE,{"derivedFrom":sQuery(id+"F0.wireOp",EDGE,"E33.3.0.38")}),1.0]])]});
            var Q39;
            Q39=makeQuery(id+"F0.imprint","IMPRINT",FACE,{"disambiguationData":[TD([[makeQuery(id+"F0.imprint","IMPRINT",EDGE,{"derivedFrom":sQuery(id+"F0.wireOp",EDGE,"E33.3.0.18")}),1.0]])]});
            var Q40;
            Q40=makeQuery(id+"F0.imprint","IMPRINT",FACE,{"disambiguationData":[TD([[makeQuery(id+"F0.imprint","IMPRINT",EDGE,{"derivedFrom":sQuery(id+"F0.wireOp",EDGE,"E33.3.0.12")}),1.0]])]});
            var Q41;
            Q41=makeQuery(id+"F0.imprint","IMPRINT",FACE,{"disambiguationData":[TD([[makeQuery(id+"F0.imprint","IMPRINT",EDGE,{"derivedFrom":sQuery(id+"F0.wireOp",EDGE,"E33.3.0.2")}),1.0]])]});
            var Q42;
            Q42=makeQuery(id+"F0.imprint","IMPRINT",FACE,{"disambiguationData":[TD([[makeQuery(id+"F0.imprint","IMPRINT",EDGE,{"derivedFrom":sQuery(id+"F0.wireOp",EDGE,"E33.3.0.17")}),-1.0]])]});
            var Q43;
            Q43=makeQuery(id+"F0.imprint","IMPRINT",FACE,{"disambiguationData":[TD([[makeQuery(id+"F0.imprint","IMPRINT",EDGE,{"derivedFrom":sQuery(id+"F0.wireOp",EDGE,"E33.3.0.41")}),1.0]])]});
            var Q44;
            Q44=makeQuery(id+"F0.imprint","IMPRINT",FACE,{"disambiguationData":[TD([[makeQuery(id+"F0.imprint","IMPRINT",EDGE,{"derivedFrom":sQuery(id+"F0.wireOp",EDGE,"E33.3.0.78")}),-1.0]])]});
            var Q45;
            Q45=makeQuery(id+"F0.imprint","IMPRINT",FACE,{"disambiguationData":[TD([[makeQuery(id+"F0.imprint","IMPRINT",EDGE,{"derivedFrom":sQuery(id+"F0.wireOp",EDGE,"E33.3.0.81")}),-1.0]])]});
            var Q46;
            Q46=makeQuery(id+"F0.imprint","IMPRINT",FACE,{"disambiguationData":[TD([[makeQuery(id+"F0.imprint","IMPRINT",EDGE,{"derivedFrom":sQuery(id+"F0.wireOp",EDGE,"E33.3.0.92")}),-1.0]])]});
            var Q47;
            Q47=makeQuery(id+"F0.imprint","IMPRINT",FACE,{"disambiguationData":[TD([[makeQuery(id+"F0.imprint","IMPRINT",EDGE,{"derivedFrom":sQuery(id+"F0.wireOp",EDGE,"E33.3.0.94")}),1.0]])]});
            var Q48;
            Q48=makeQuery(id+"F0.imprint","IMPRINT",FACE,{"disambiguationData":[TD([[makeQuery(id+"F0.imprint","IMPRINT",EDGE,{"derivedFrom":sQuery(id+"F0.wireOp",EDGE,"E33.3.0.95")}),1.0]])]});
            var Q49;
            Q49=makeQuery(id+"F0.imprint","IMPRINT",FACE,{"disambiguationData":[TD([[makeQuery(id+"F0.imprint","IMPRINT",EDGE,{"derivedFrom":sQuery(id+"F0.wireOp",EDGE,"E33.3.0.93")}),1.0]])]});
            var Q50;
            Q50=makeQuery(id+"F0.imprint","IMPRINT",FACE,{"disambiguationData":[TD([[makeQuery(id+"F0.imprint","IMPRINT",EDGE,{"derivedFrom":sQuery(id+"F0.wireOp",EDGE,"E33.4.0.95")}),1.0]])]});
            var Q51;
            Q51=makeQuery(id+"F0.imprint","IMPRINT",FACE,{"disambiguationData":[TD([[makeQuery(id+"F0.imprint","IMPRINT",EDGE,{"derivedFrom":sQuery(id+"F0.wireOp",EDGE,"E33.4.0.94")}),1.0]])]});
            var Q52;
            Q52=makeQuery(id+"F0.imprint","IMPRINT",FACE,{"disambiguationData":[TD([[makeQuery(id+"F0.imprint","IMPRINT",EDGE,{"derivedFrom":sQuery(id+"F0.wireOp",EDGE,"E33.4.0.92")}),-1.0]])]});
            var Q53;
            Q53=makeQuery(id+"F0.imprint","IMPRINT",FACE,{"disambiguationData":[TD([[makeQuery(id+"F0.imprint","IMPRINT",EDGE,{"derivedFrom":sQuery(id+"F0.wireOp",EDGE,"E33.4.0.81")}),-1.0]])]});
            var Q54;
            Q54=makeQuery(id+"F0.imprint","IMPRINT",FACE,{"disambiguationData":[TD([[makeQuery(id+"F0.imprint","IMPRINT",EDGE,{"derivedFrom":sQuery(id+"F0.wireOp",EDGE,"E33.4.0.78")}),-1.0]])]});
            var Q55;
            Q55=makeQuery(id+"F0.imprint","IMPRINT",FACE,{"disambiguationData":[TD([[makeQuery(id+"F0.imprint","IMPRINT",EDGE,{"derivedFrom":sQuery(id+"F0.wireOp",EDGE,"E33.4.0.41")}),1.0]])]});
            var Q56;
            Q56=makeQuery(id+"F0.imprint","IMPRINT",FACE,{"disambiguationData":[TD([[makeQuery(id+"F0.imprint","IMPRINT",EDGE,{"derivedFrom":sQuery(id+"F0.wireOp",EDGE,"E33.4.0.17")}),-1.0]])]});
            var Q57;
            Q57=makeQuery(id+"F0.imprint","IMPRINT",FACE,{"disambiguationData":[TD([[makeQuery(id+"F0.imprint","IMPRINT",EDGE,{"derivedFrom":sQuery(id+"F0.wireOp",EDGE,"E33.4.0.2")}),1.0]])]});
            var Q58;
            {var subQ1=sQuery(id+"F0.wireOp",EDGE,"E33.4.0.11");Q58=makeQuery(id+"F0.imprint","IMPRINT",FACE,{"disambiguationData":[TD([[makeQuery(id+"F0.imprint","IMPRINT",EDGE,{"derivedFrom":subQ1}),1.0]])]});}
            var Q59;
            Q59=makeQuery(id+"F0.imprint","IMPRINT",FACE,{"disambiguationData":[TD([[makeQuery(id+"F0.imprint","IMPRINT",EDGE,{"derivedFrom":sQuery(id+"F0.wireOp",EDGE,"E33.4.0.37")}),1.0]])]});
            var Q60;
            Q60=makeQuery(id+"F0.imprint","IMPRINT",FACE,{"disambiguationData":[TD([[makeQuery(id+"F0.imprint","IMPRINT",EDGE,{"derivedFrom":sQuery(id+"F0.wireOp",EDGE,"E33.4.0.40")}),1.0]])]});
            var Q61;
            Q61=makeQuery(id+"F0.imprint","IMPRINT",FACE,{"disambiguationData":[TD([[makeQuery(id+"F0.imprint","IMPRINT",EDGE,{"derivedFrom":sQuery(id+"F0.wireOp",EDGE,"E105")}),-1.0]])]});
            var Q62;
            Q62=makeQuery(id+"F0.imprint","IMPRINT",FACE,{"disambiguationData":[TD([[makeQuery(id+"F0.imprint","IMPRINT",EDGE,{"derivedFrom":sQuery(id+"F0.wireOp",EDGE,"E33.4.0.25")}),1.0]])]});
            var Q63;
            Q63=makeQuery(id+"F0.imprint","IMPRINT",FACE,{"disambiguationData":[TD([[makeQuery(id+"F0.imprint","IMPRINT",EDGE,{"derivedFrom":sQuery(id+"F0.wireOp",EDGE,"E33.4.0.93")}),1.0]])]});
            var Q64;
            Q64=makeQuery(id+"F0.imprint","IMPRINT",FACE,{"disambiguationData":[TD([[makeQuery(id+"F0.imprint","IMPRINT",EDGE,{"derivedFrom":sQuery(id+"F0.wireOp",EDGE,"E111")}),-1.0]])]});
            var Q65;
            Q65=makeQuery(id+"F0.imprint","IMPRINT",FACE,{"disambiguationData":[TD([[makeQuery(id+"F0.imprint","IMPRINT",EDGE,{"derivedFrom":sQuery(id+"F0.wireOp",EDGE,"E7.2")}),1.0]])]});
            extrude(context, id + "F3", {"entities" : qUnion([Q0, Q1, Q2, Q3, Q4, Q5, Q6, Q7, Q8, Q9, Q10, Q11, Q12, Q13, Q14, Q15, Q16, Q17, Q18, Q19, Q20, Q21, Q22, Q23, Q24, Q25, Q26, Q27, Q28, Q29, Q30, Q31, Q32, Q33, Q34, Q35, Q36, Q37, Q38, Q39, Q40, Q41, Q42, Q43, Q44, Q45, Q46, Q47, Q48, Q49, Q50, Q51, Q52, Q53, Q54, Q55, Q56, Q57, Q58, Q59, Q60, Q61, Q62, Q63, Q64, Q65]), "operationType" : NewBodyOperationType.REMOVE, "oppositeDirection" : true, "depth" : 0.8 * mm, "offsetDistance" : 25.4 * mm});
        }
        {
            var Q0;
            Q0=makeQuery(id+"F2.opExtrude","SWEPT_FACE",FACE,{"disambiguationData":[OSD([sQuery(id+"F1.wireOp",EDGE,"E155.right")])]});
            var sketch = newSketch(context, id + "F4", { "sketchPlane" : qUnion([Q0])});
            skLineSegment(sketch, "E156", {"start": v(-30.17, -34.5) * mm, "end": v(32.15, -34.5) * mm, "construction": true});
            skLineSegment(sketch, "E157", {"start": v(0, -23.35) * mm, "end": v(0, -27.7) * mm, "construction": true});
            skLineSegment(sketch, "E158", {"start": v(0, -56.14) * mm, "end": v(0, -23.35) * mm, "construction": true});
            skFitSpline(sketch, "E159.MirrorCS", {"points": [v(-30.17, -34.5) * mm, v(-26.64, -39.01) * mm, v(-9.21, -44.76) * mm, v(0, -45.65) * mm, v(0, -45.68) * mm], "startDerivative": vector(14.52, -20.81) * mm, "endDerivative": vector(-0.75, -1.6) * mm});
            skFitSpline(sketch, "E160", {"points": [v(0, -23.35) * mm, v(9.18, -24.36) * mm, v(17.06, -30.9) * mm, v(17.86, -39.85) * mm, v(15.89, -43.42) * mm, v(0, -45.67) * mm], "startDerivative": vector(47.62, 0.61) * mm, "endDerivative": vector(-68.98, -2.9) * mm});
            skPoint(sketch, "E161", {"position": v(0, -34.5) * mm});
            skEllipticalArc(sketch, "E162", {});
            skCircle(sketch, "E163", {"center": v(0, -34.5) * mm, "radius": 3.77 * mm});
            skFitSpline(sketch, "E164", {"points": [v(-30.17, -34.5) * mm, v(-26.64, -30) * mm, v(-6.52, -27) * mm, v(5.33, -27.7) * mm, v(13.89, -30) * mm, v(17.06, -30.9) * mm], "startDerivative": vector(12.77, 31.47) * mm, "endDerivative": vector(22.99, -6.27) * mm});
            skFitSpline(sketch, "E165.trimOffspring", {"points": [v(-30.17, -34.5) * mm, v(-26.64, -30) * mm, v(-9.21, -24.25) * mm, v(0, -23.36) * mm, v(0, -23.34) * mm], "startDerivative": vector(14.52, 20.81) * mm, "endDerivative": vector(-0.75, 1.6) * mm});
            skEllipticalArc(sketch, "E166.trimOffspring", {});
            skEllipse(sketch, "E167", {"center": v(1.69, -32.5) * mm, "majorRadius": 0.86 * mm, "minorRadius": 0.38 * mm, "majorAxis": v(-0.8, 0.6)});
            skEllipse(sketch, "E168", {"center": v(2.84, -34.5) * mm, "majorRadius": 0.8 * mm, "minorRadius": 0.27 * mm, "majorAxis": v(0.22, -0.98)});
            skFitSpline(sketch, "E169", {"points": [v(-9.4, -27.8) * mm, v(-10.2, -28.93) * mm, v(-3.42, -31.93) * mm, v(-9.24, -29.1) * mm, v(-9.4, -27.8) * mm]});
            skFitSpline(sketch, "E170", {"points": [v(-10.48, -36.62) * mm, v(-10.37, -35.66) * mm, v(-4.32, -35.6) * mm, v(-9.75, -36.28) * mm, v(-9.97, -37.47) * mm, v(-10.48, -36.62) * mm]});
            skFitSpline(sketch, "E171", {"points": [v(-11.27, -30.86) * mm, v(-11.61, -32.5) * mm, v(-10.14, -32.21) * mm, v(-8.79, -32.83) * mm, v(-9.13, -31.65) * mm, v(-10.48, -31.48) * mm, v(-11.27, -30.86) * mm]});
            skFitSpline(sketch, "E172", {"points": [v(3.87, -31.99) * mm, v(8, -30.57) * mm, v(7.94, -29.56) * mm, v(9.07, -31.2) * mm, v(3.87, -31.99) * mm]});
            skFitSpline(sketch, "E173", {"points": [v(3.76, -36.56) * mm, v(8, -39.1) * mm, v(7.55, -39.5) * mm, v(3.76, -36.56) * mm]});
            skFitSpline(sketch, "E174", {"points": [v(2.06, -38.77) * mm, v(2.97, -41.88) * mm, v(2.8, -40.3) * mm, v(2.06, -38.77) * mm]});
            skPoint(sketch, "E175.0.internal.snap0", {"position": v(0, -39.74) * mm});
            skPoint(sketch, "E175.2.internal.snap0", {"position": v(0, -39.74) * mm});
            skFitSpline(sketch, "E175", {"points": [v(-6.6, -39.74) * mm, v(-4.4, -38.07) * mm, v(-4.03, -39.74) * mm, v(-6.6, -39.74) * mm]});
            skFitSpline(sketch, "E176.0", {"points": [v(-29.23, -34.89) * mm, v(-29.1, -34.56) * mm, v(-28.84, -33.93) * mm, v(-28.41, -33.06) * mm, v(-27.9, -32.28) * mm, v(-27.33, -31.7) * mm, v(-26.74, -31.25) * mm, v(-26.23, -30.93) * mm, v(-25.63, -30.62) * mm, v(-24.7, -30.23) * mm, v(-23.3, -29.8) * mm, v(-21.38, -29.34) * mm, v(-19.24, -28.97) * mm, v(-16.97, -28.68) * mm, v(-14.63, -28.44) * mm, v(-12.26, -28.27) * mm, v(-9.93, -28.14) * mm, v(-7.7, -28.05) * mm, v(-5.64, -28) * mm, v(-3.76, -27.97) * mm, v(-2.05, -27.98) * mm, v(0.08, -28.05) * mm, v(2.5, -28.24) * mm, v(5.29, -28.69) * mm, v(8.24, -29.4) * mm, v(10.6, -30.07) * mm, v(12.3, -30.59) * mm, v(13.45, -30.93) * mm, v(14.44, -31.23) * mm, v(15.59, -31.55) * mm, v(16.31, -31.75) * mm, v(16.79, -31.88) * mm]});
            skFitSpline(sketch, "E176.1", {"points": [v(-29.33, -33.93) * mm, v(-29.01, -34.39) * mm, v(-28.47, -35.26) * mm, v(-27.78, -36.4) * mm, v(-27.01, -37.38) * mm, v(-25.96, -38.31) * mm, v(-24.34, -39.3) * mm, v(-22.26, -40.28) * mm, v(-19.82, -41.2) * mm, v(-17.14, -42.04) * mm, v(-14.3, -42.78) * mm, v(-11.88, -43.29) * mm, v(-9.96, -43.62) * mm, v(-8.54, -43.84) * mm, v(-7.14, -44.01) * mm, v(-5.8, -44.16) * mm, v(-4.54, -44.27) * mm, v(-3.39, -44.36) * mm, v(-2.52, -44.42) * mm, v(-1.9, -44.46) * mm, v(-1.49, -44.48) * mm, v(-1.1, -44.5) * mm, v(-0.77, -44.53) * mm, v(-0.52, -44.55) * mm, v(-0.35, -44.57) * mm, v(-0.23, -44.58) * mm, v(-0.12, -44.6) * mm, v(-0.02, -44.6) * mm, v(0.07, -44.62) * mm, v(0.15, -44.63) * mm, v(0.2, -44.65) * mm, v(0.28, -44.67) * mm, v(0.37, -44.7) * mm, v(0.46, -44.74) * mm, v(0.54, -44.79) * mm, v(0.64, -44.86) * mm, v(0.77, -44.98) * mm, v(0.9, -45.16) * mm, v(1, -45.39) * mm, v(1.03, -45.62) * mm, v(1.02, -45.8) * mm, v(0.98, -45.94) * mm, v(0.94, -46.07) * mm, v(0.92, -46.1) * mm, v(0.92, -46.11) * mm]});
            skFitSpline(sketch, "E176.2", {"points": [v(0.02, -24.36) * mm, v(1, -24.35) * mm, v(2.93, -24.33) * mm, v(5.22, -24.48) * mm, v(7.02, -24.78) * mm, v(8.35, -25.13) * mm, v(9.68, -25.62) * mm, v(11, -26.25) * mm, v(12.28, -27.02) * mm, v(13.47, -27.92) * mm, v(14.52, -28.93) * mm, v(15.27, -29.85) * mm, v(15.77, -30.63) * mm, v(16.1, -31.23) * mm, v(16.37, -31.85) * mm, v(16.67, -32.73) * mm, v(16.93, -33.87) * mm, v(17.1, -35.29) * mm, v(17.12, -36.7) * mm, v(17.06, -38.05) * mm, v(16.94, -39.1) * mm, v(16.83, -39.86) * mm, v(16.72, -40.54) * mm, v(16.54, -41.23) * mm, v(16.3, -41.71) * mm, v(16.04, -42.03) * mm, v(15.8, -42.26) * mm, v(15.47, -42.5) * mm, v(15.05, -42.72) * mm, v(14.51, -42.94) * mm, v(13.67, -43.23) * mm, v(12.41, -43.54) * mm, v(10.64, -43.85) * mm, v(8, -44.18) * mm, v(4.37, -44.46) * mm, v(1.4, -44.6) * mm, v(-0.04, -44.66) * mm]});
            const initialGuessF4  = {"E162": [4.020296512066982e-06, -0.034508027136325836, -0.9801563531494704, 0.19822594023167323, 0.01408274269422727, 0.009251013711509068, 5.861168892050575, 3.9026843157575417], "E166.trimOffspring": [4.020296512066982e-06, -0.034508027136325836, -0.9801563531494704, 0.19822594023167323, 0.01408274269422727, 0.009251013711509068, 4.844467289809227, 4.844587133916803]};
            skSetInitialGuess(sketch, initialGuessF4);
            skSolve(sketch);
        }
        {
            var Q0;
            {var subQ1=sQuery(id+"F4.wireOp",EDGE,"E162");Q0=makeQuery(id+"F4.imprint","IMPRINT",FACE,{"disambiguationData":[TD([[makeQuery(id+"F4.imprint","IMPRINT",EDGE,{"derivedFrom":subQ1}),-1.0]])]});}
            var Q1;
            Q1=makeQuery(id+"F4.imprint","IMPRINT",FACE,{"disambiguationData":[TD([[makeQuery(id+"F4.imprint","IMPRINT",EDGE,{"derivedFrom":sQuery(id+"F4.wireOp",EDGE,"E171")}),1.0]])]});
            var Q2;
            {var subQ1=sQuery(id+"F4.wireOp",EDGE,"E169");var subQ3=makeQuery(id+"F4.imprint","IMPRINT",VERTEX,{"derivedFrom":subQ1});Q2=makeQuery(id+"F4.imprint","IMPRINT",FACE,{"disambiguationData":[TD([[makeQuery(id+"F4.imprint","IMPRINT",EDGE,{"disambiguationData":[TD([[subQ3,1.0]])],"derivedFrom":subQ1}),1.0]])]});}
            var Q3;
            Q3=makeQuery(id+"F4.imprint","IMPRINT",FACE,{"disambiguationData":[TD([[makeQuery(id+"F4.imprint","IMPRINT",EDGE,{"derivedFrom":sQuery(id+"F4.wireOp",EDGE,"E170")}),-1.0]])]});
            var Q4;
            Q4=makeQuery(id+"F4.imprint","IMPRINT",FACE,{"disambiguationData":[TD([[makeQuery(id+"F4.imprint","IMPRINT",EDGE,{"derivedFrom":sQuery(id+"F4.wireOp",EDGE,"E175")}),-1.0]])]});
            var Q5;
            Q5=makeQuery(id+"F4.imprint","IMPRINT",FACE,{"disambiguationData":[TD([[makeQuery(id+"F4.imprint","IMPRINT",EDGE,{"derivedFrom":sQuery(id+"F4.wireOp",EDGE,"E174")}),1.0]])]});
            var Q6;
            Q6=makeQuery(id+"F4.imprint","IMPRINT",FACE,{"disambiguationData":[TD([[makeQuery(id+"F4.imprint","IMPRINT",EDGE,{"derivedFrom":sQuery(id+"F4.wireOp",EDGE,"E173")}),-1.0]])]});
            var Q7;
            Q7=makeQuery(id+"F4.imprint","IMPRINT",FACE,{"disambiguationData":[TD([[makeQuery(id+"F4.imprint","IMPRINT",EDGE,{"derivedFrom":sQuery(id+"F4.wireOp",EDGE,"E172")}),-1.0]])]});
            var Q8;
            Q8=makeQuery(id+"F4.imprint","IMPRINT",FACE,{"disambiguationData":[TD([[makeQuery(id+"F4.imprint","IMPRINT",EDGE,{"derivedFrom":sQuery(id+"F4.wireOp",EDGE,"E163")}),1.0]])]});
            extrude(context, id + "F5", {"entities" : qUnion([Q0, Q1, Q2, Q3, Q4, Q5, Q6, Q7, Q8]), "operationType" : NewBodyOperationType.REMOVE, "oppositeDirection" : true, "depth" : 0.8 * mm, "offsetDistance" : 25.4 * mm});
        }
        {
            var Q0;
            {var subQ7=sQuery(id+"F1.wireOp",EDGE,"E155.bottom");var subQ8=sQuery(id+"F1.wireOp",EDGE,"E155.right");Q0=makeQuery(id+"F5.boolean.opBoolean","SPLIT",FACE,{"disambiguationData":[TD([makeQuery(id+"F2.opExtrude","SWEPT_FACE",FACE,{"disambiguationData":[OSD([subQ7])]})])],"derivedFrom":makeQuery(id+"F2.opExtrude","SWEPT_FACE",FACE,{"disambiguationData":[OSD([subQ8])]})});}
            var sketch = newSketch(context, id + "F6", { "sketchPlane" : qUnion([Q0])});
            skFitSpline(sketch, "E177.0", {"points": [v(-29.7, -34.7) * mm, v(-29.56, -34.37) * mm, v(-29.3, -33.73) * mm, v(-28.86, -32.81) * mm, v(-28.3, -31.96) * mm, v(-27.54, -31.18) * mm, v(-26.7, -30.6) * mm, v(-25.84, -30.16) * mm, v(-24.86, -29.75) * mm, v(-23.44, -29.3) * mm, v(-21.48, -28.85) * mm, v(-19.32, -28.47) * mm, v(-17.03, -28.17) * mm, v(-14.67, -27.94) * mm, v(-12.3, -27.76) * mm, v(-9.96, -27.63) * mm, v(-7.72, -27.55) * mm, v(-5.65, -27.5) * mm, v(-3.77, -27.46) * mm, v(-2.04, -27.47) * mm, v(0.1, -27.54) * mm, v(2.56, -27.73) * mm, v(5.4, -28.19) * mm, v(8.37, -28.9) * mm, v(10.74, -29.59) * mm, v(12.44, -30.1) * mm, v(13.6, -30.45) * mm, v(14.58, -30.74) * mm, v(15.72, -31.06) * mm, v(16.44, -31.26) * mm, v(16.92, -31.4) * mm]});
            skFitSpline(sketch, "E177.1", {"points": [v(-29.75, -34.22) * mm, v(-29.44, -34.66) * mm, v(-28.9, -35.52) * mm, v(-28.2, -36.67) * mm, v(-27.39, -37.72) * mm, v(-26.26, -38.73) * mm, v(-24.57, -39.76) * mm, v(-22.45, -40.75) * mm, v(-19.99, -41.68) * mm, v(-17.28, -42.53) * mm, v(-14.41, -43.27) * mm, v(-11.49, -43.89) * mm, v(-9.07, -44.28) * mm, v(-7.2, -44.52) * mm, v(-5.85, -44.66) * mm, v(-4.59, -44.78) * mm, v(-3.42, -44.87) * mm, v(-2.56, -44.92) * mm, v(-1.94, -44.96) * mm, v(-1.52, -45) * mm, v(-1.14, -45.02) * mm, v(-0.8, -45.04) * mm, v(-0.52, -45.06) * mm, v(-0.32, -45.08) * mm, v(-0.18, -45.1) * mm, v(-0.09, -45.1) * mm, v(-0.02, -45.12) * mm, v(0.04, -45.13) * mm, v(0.08, -45.14) * mm, v(0.13, -45.15) * mm, v(0.18, -45.17) * mm, v(0.25, -45.2) * mm, v(0.32, -45.26) * mm, v(0.39, -45.32) * mm, v(0.45, -45.41) * mm, v(0.5, -45.52) * mm, v(0.52, -45.64) * mm, v(0.5, -45.74) * mm, v(0.5, -45.8) * mm, v(0.48, -45.85) * mm, v(0.47, -45.87) * mm, v(0.47, -45.88) * mm, v(0.46, -45.88) * mm, v(0.46, -45.89) * mm, v(0.46, -45.89) * mm, v(0.46, -45.9) * mm]});
            skFitSpline(sketch, "E177.2", {"points": [v(0.01, -23.85) * mm, v(1, -23.84) * mm, v(2.94, -23.82) * mm, v(5.28, -23.97) * mm, v(7.12, -24.29) * mm, v(8.5, -24.64) * mm, v(9.88, -25.15) * mm, v(11.25, -25.8) * mm, v(12.57, -26.6) * mm, v(13.8, -27.53) * mm, v(14.9, -28.58) * mm, v(15.84, -29.74) * mm, v(16.58, -31) * mm, v(17.1, -32.35) * mm, v(17.43, -33.79) * mm, v(17.6, -35.25) * mm, v(17.63, -36.7) * mm, v(17.56, -38.1) * mm, v(17.45, -39.16) * mm, v(17.33, -39.93) * mm, v(17.21, -40.64) * mm, v(17.02, -41.4) * mm, v(16.68, -42.1) * mm, v(16.24, -42.57) * mm, v(15.74, -42.93) * mm, v(15.1, -43.27) * mm, v(14.07, -43.65) * mm, v(12.51, -44.04) * mm, v(10.71, -44.35) * mm, v(8.06, -44.69) * mm, v(4.4, -44.97) * mm, v(1.42, -45.1) * mm, v(-0.02, -45.16) * mm]});
            skFitSpline(sketch, "E177.3", {"points": [v(-29.7, -34.7) * mm, v(-29.56, -34.37) * mm, v(-29.3, -33.73) * mm, v(-28.86, -32.81) * mm, v(-28.3, -31.96) * mm, v(-27.54, -31.18) * mm, v(-26.7, -30.6) * mm, v(-25.84, -30.16) * mm, v(-24.86, -29.75) * mm, v(-23.44, -29.3) * mm, v(-21.48, -28.85) * mm, v(-19.32, -28.47) * mm, v(-17.03, -28.17) * mm, v(-14.67, -27.94) * mm, v(-12.3, -27.76) * mm, v(-9.96, -27.63) * mm, v(-7.72, -27.55) * mm, v(-5.65, -27.5) * mm, v(-3.77, -27.46) * mm, v(-2.04, -27.47) * mm, v(0.1, -27.54) * mm, v(2.56, -27.73) * mm, v(5.4, -28.19) * mm, v(8.37, -28.9) * mm, v(10.74, -29.59) * mm, v(12.44, -30.1) * mm, v(13.6, -30.45) * mm, v(14.58, -30.74) * mm, v(15.72, -31.06) * mm, v(16.44, -31.26) * mm, v(16.92, -31.4) * mm]});
            skFitSpline(sketch, "E178.trimOffspring", {"points": [v(-29.6, -34.45) * mm, v(-28.83, -32.82) * mm, v(-27.97, -31.65) * mm, v(-25.86, -30.18) * mm, v(-23.88, -29.45) * mm, v(-22.38, -29.06) * mm, v(-20.35, -28.66) * mm, v(-18.01, -28.3) * mm, v(-16.22, -28.1) * mm, v(-11.87, -27.74) * mm, v(-4.25, -27.4) * mm, v(11.4, -29.79) * mm, v(13.64, -30.46) * mm, v(16.7, -31.33) * mm], "startDerivative": vector(13.32, 29.87) * mm, "endDerivative": vector(44.29, -12.49) * mm});
            skFitSpline(sketch, "E179.trimOffspring", {"points": [v(-29.7, -34.7) * mm, v(-29.56, -34.37) * mm, v(-29.3, -33.73) * mm, v(-28.86, -32.81) * mm, v(-28.3, -31.96) * mm, v(-27.54, -31.18) * mm, v(-26.7, -30.6) * mm, v(-25.84, -30.16) * mm, v(-24.86, -29.75) * mm, v(-23.44, -29.3) * mm, v(-21.48, -28.85) * mm, v(-19.32, -28.47) * mm, v(-17.03, -28.17) * mm, v(-14.67, -27.94) * mm, v(-12.3, -27.76) * mm, v(-9.96, -27.63) * mm, v(-7.72, -27.55) * mm, v(-5.65, -27.5) * mm, v(-3.77, -27.46) * mm, v(-2.04, -27.47) * mm, v(0.1, -27.54) * mm, v(2.56, -27.73) * mm, v(5.4, -28.19) * mm, v(8.37, -28.9) * mm, v(10.74, -29.59) * mm, v(12.44, -30.1) * mm, v(13.6, -30.45) * mm, v(14.58, -30.74) * mm, v(15.72, -31.06) * mm, v(16.44, -31.26) * mm, v(16.92, -31.4) * mm]});
            skFitSpline(sketch, "E180.0", {"points": [v(-28.92, -35.01) * mm, v(-28.79, -34.69) * mm, v(-28.53, -34.06) * mm, v(-28.12, -33.22) * mm, v(-27.63, -32.49) * mm, v(-27.1, -31.94) * mm, v(-26.56, -31.52) * mm, v(-26.07, -31.22) * mm, v(-25.5, -30.92) * mm, v(-24.58, -30.55) * mm, v(-23.22, -30.11) * mm, v(-21.31, -29.67) * mm, v(-19.2, -29.3) * mm, v(-16.94, -29) * mm, v(-14.6, -28.77) * mm, v(-12.24, -28.6) * mm, v(-9.92, -28.47) * mm, v(-7.7, -28.38) * mm, v(-5.63, -28.33) * mm, v(-3.76, -28.3) * mm, v(-2.05, -28.31) * mm, v(0.06, -28.38) * mm, v(2.46, -28.57) * mm, v(5.22, -29.01) * mm, v(8.15, -29.72) * mm, v(10.5, -30.4) * mm, v(12.2, -30.9) * mm, v(13.35, -31.25) * mm, v(14.35, -31.54) * mm, v(15.5, -31.87) * mm, v(16.22, -32.07) * mm, v(16.7, -32.2) * mm]});
            skFitSpline(sketch, "E180.1", {"points": [v(-29.06, -33.74) * mm, v(-28.74, -34.2) * mm, v(-28.19, -35.1) * mm, v(-27.5, -36.2) * mm, v(-26.9, -37) * mm, v(-26.27, -37.6) * mm, v(-25.5, -38.2) * mm, v(-24.19, -39.01) * mm, v(-22.13, -39.97) * mm, v(-19.72, -40.88) * mm, v(-17.05, -41.72) * mm, v(-14.22, -42.45) * mm, v(-11.81, -42.96) * mm, v(-9.9, -43.3) * mm, v(-8.5, -43.51) * mm, v(-7.1, -43.69) * mm, v(-5.77, -43.83) * mm, v(-4.52, -43.94) * mm, v(-3.55, -44.01) * mm, v(-2.85, -44.06) * mm, v(-2.35, -44.1) * mm, v(-1.89, -44.13) * mm, v(-1.46, -44.15) * mm, v(-1.08, -44.18) * mm, v(-0.74, -44.2) * mm, v(-0.5, -44.22) * mm, v(-0.32, -44.24) * mm, v(-0.2, -44.25) * mm, v(-0.08, -44.26) * mm, v(0.03, -44.28) * mm, v(0.13, -44.3) * mm, v(0.22, -44.31) * mm, v(0.3, -44.33) * mm, v(0.39, -44.36) * mm, v(0.5, -44.4) * mm, v(0.6, -44.45) * mm, v(0.72, -44.5) * mm, v(0.83, -44.59) * mm, v(0.94, -44.68) * mm, v(1.05, -44.8) * mm, v(1.2, -45) * mm, v(1.31, -45.3) * mm, v(1.36, -45.6) * mm, v(1.34, -45.85) * mm, v(1.3, -46.03) * mm, v(1.25, -46.2) * mm, v(1.22, -46.24) * mm, v(1.22, -46.25) * mm]});
            skFitSpline(sketch, "E180.2", {"points": [v(0.02, -24.7) * mm, v(1.01, -24.68) * mm, v(2.93, -24.66) * mm, v(5.19, -24.8) * mm, v(6.95, -25.1) * mm, v(8.25, -25.45) * mm, v(9.55, -25.92) * mm, v(10.85, -26.54) * mm, v(12.1, -27.3) * mm, v(13.25, -28.17) * mm, v(14.28, -29.15) * mm, v(15, -30.04) * mm, v(15.49, -30.8) * mm, v(15.8, -31.37) * mm, v(16.06, -31.97) * mm, v(16.35, -32.81) * mm, v(16.6, -33.92) * mm, v(16.76, -35.3) * mm, v(16.8, -36.69) * mm, v(16.73, -38.02) * mm, v(16.61, -39.05) * mm, v(16.5, -39.8) * mm, v(16.42, -40.3) * mm, v(16.32, -40.73) * mm, v(16.22, -41.09) * mm, v(16.1, -41.37) * mm, v(15.96, -41.6) * mm, v(15.8, -41.8) * mm, v(15.6, -42) * mm, v(15.3, -42.2) * mm, v(14.9, -42.42) * mm, v(14.4, -42.63) * mm, v(13.58, -42.9) * mm, v(12.35, -43.22) * mm, v(10.6, -43.52) * mm, v(8.63, -43.77) * mm, v(6.53, -43.96) * mm, v(3.61, -44.16) * mm, v(1.38, -44.27) * mm, v(-0.05, -44.33) * mm]});
            skLineSegment(sketch, "E181.0", {"start": v(44.45, -82.55) * mm, "end": v(44.45, 6.35) * mm});
            skLineSegment(sketch, "E181.1", {"start": v(-44.45, -82.55) * mm, "end": v(44.45, -82.55) * mm});
            skLineSegment(sketch, "E181.2", {"start": v(-44.45, 6.35) * mm, "end": v(-44.45, -82.55) * mm});
            skLineSegment(sketch, "E181.3", {"start": v(44.45, 6.35) * mm, "end": v(-44.45, 6.35) * mm});
            skSolve(sketch);
        }
        {
            var Q0;
            Q0=makeQuery(id+"F6.imprint","IMPRINT",FACE,{"disambiguationData":[TD([[makeQuery(id+"F6.imprint","IMPRINT",EDGE,{"derivedFrom":sQuery(id+"F6.wireOp",EDGE,"E177.0")}),-1.0]])]});
            extrude(context, id + "F7", {"entities" : qUnion([Q0]), "operationType" : NewBodyOperationType.ADD, "depth" : 0.8 * mm, "offsetDistance" : 25.4 * mm, "hasSecondDirection" : true, "secondDirectionOppositeDirection" : true, "secondDirectionDepth" : 25.4 * mm});
        }
    });
